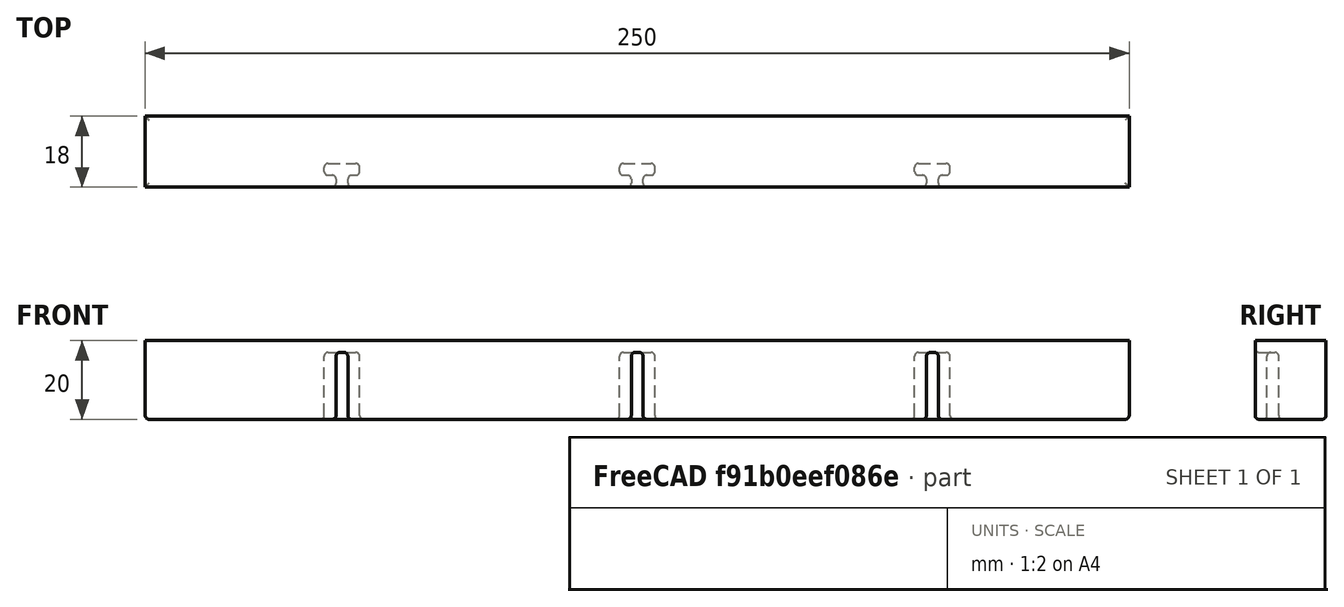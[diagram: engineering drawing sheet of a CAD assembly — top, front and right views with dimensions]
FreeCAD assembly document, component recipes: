
FREECAD ASSEMBLY — COMPONENT RECIPES ("Rack")

This assembly document has 20 components, labeled P0..P19 below (a component is one placed body or linked part). 20 of them carry a construction recipe — the FreeCAD feature program that regenerates the part from scratch, quoted from this document or its linked companion documents; the rest are supplied as boundary geometry only. No exploded tour is included for this assembly.
COMPONENT P0 — recipe-attached ("CenterPanelBottom001", modeled in this document).
Construction recipe (the document's own serialized feature program — sketch geometry with constraints, then the solid features built on it; lengths are millimeters unless a unit is written):

FEATURE [PartDesign::SubShapeBinder] Binder012  label="BinderCenterPanelBottom"
  BindCopyOnChange = 0
  BindMode = 0
  ClaimChildren = false
  Context = -> Body007 [Binder012.]
  Fuse = false
  MakeFace = true
  OffsetFill = false
  OffsetIntersection = false
  OffsetJoinType = 0
  OffsetOpenResult = false
  PartialLoad = false
  Refine = true
  Relative = true
  Support = -> [Sketch]
  _Version = 2
FEATURE [Sketcher::SketchObject] Sketch032  label="SketchCenterPanelBottom"
  ArcFitTolerance = 1e-06
  AttachmentSupport = -> [Origin016]
  ExternalGeometry = -> [Binder012]
  ExternalTypes = [0,0,0,0,0,0]
  FullyConstrained = true
  MakeInternals = false
  MapMode = 5
  sketch-geometry (13):
    g0: LineSegment StartX=-25 StartY=100 StartZ=0 EndX=-25 EndY=-100 EndZ=0
    g1: LineSegment StartX=-25 StartY=-100 StartZ=0 EndX=25 EndY=-100 EndZ=0
    g2: LineSegment StartX=25 StartY=-100 StartZ=0 EndX=25 EndY=100 EndZ=0
    g3: LineSegment StartX=25 StartY=100 StartZ=0 EndX=-25 EndY=100 EndZ=0
    g4: LineSegment [constr] StartX=-20 StartY=-95 StartZ=0 EndX=20 EndY=-95 EndZ=0
    g5: LineSegment [constr] StartX=20 StartY=-95 StartZ=0 EndX=20 EndY=95 EndZ=0
    g6: LineSegment [constr] StartX=20 StartY=95 StartZ=0 EndX=-20 EndY=95 EndZ=0
    g7: LineSegment [constr] StartX=-20 StartY=95 StartZ=0 EndX=-20 EndY=-95 EndZ=0
    g8: GeomPoint [constr] X=0 Y=0 Z=0
    g9: GeomPoint X=-20 Y=95 Z=0
    g10: GeomPoint X=20 Y=95 Z=0
    g11: GeomPoint X=20 Y=-95 Z=0
    g12: GeomPoint X=-20 Y=-95 Z=0
  constraints (26):
    c: Coincident(g0,g1)
    c: Coincident(g1,g2)
    c: Coincident(g2,g3)
    c: Coincident(g3,g0)
    c: Vertical(g0)
    c: Vertical(g2)
    c: Horizontal(g1)
    c: Horizontal(g3)
    c: Coincident(g0,g-7)
    c: Coincident(g1,g-8)
    c: Coincident(g4,g5)
    c: Coincident(g5,g6)
    c: Coincident(g6,g7)
    c: Coincident(g7,g4)
    c: Horizontal(g4)
    c: Horizontal(g6)
    c: Vertical(g5)
    c: Vertical(g7)
    c: Symmetric(g6,g4,g8)
    c: Coincident(g8,g-1)
    c: Distance(g3,g6) = 5
    c: Distance(g2,g5) = 5
    c: Coincident(g9,g6)
    c: Coincident(g10,g5)
    c: Coincident(g11,g4)
    c: Coincident(g12,g4)
FEATURE [PartDesign::Pad] Pad012  label="PadCenterPanelBottom"
  Direction = (0,0,1)
  Length = 20
  Length2 = 10
  Profile = -> Sketch032
  ReferenceAxis = -> Sketch032 [N_Axis]
  Refine = true
  Reversed = true
  SideType = 0
  Suppressed = false
  Type = 0
  Type2 = 0
FEATURE [Sketcher::SketchObject] Sketch033  label="SketchCenterPanelBottomJoints"
  ArcFitTolerance = 1e-06
  AttachmentSupport = -> [Pad012]
  ExternalGeometry = -> [Sketch032]
  ExternalTypes = [0,0,0,0]
  FullyConstrained = true
  MakeInternals = false
  MapMode = 5
  sketch-geometry (40):
    g0: GeomPoint [constr] X=-1.3e-15 Y=100 Z=0
    g1: GeomPoint [constr] X=-4e-16 Y=-100 Z=0
    g2: LineSegment [constr] StartX=-1.5 StartY=100 StartZ=0 EndX=-1.5 EndY=97 EndZ=0
    g3: LineSegment [constr] StartX=-1.5 StartY=97 StartZ=0 EndX=1.5 EndY=97 EndZ=0
    g4: LineSegment [constr] StartX=1.5 StartY=97 StartZ=0 EndX=1.5 EndY=100 EndZ=0
    g5: LineSegment [constr] StartX=1.5 StartY=100 StartZ=0 EndX=-1.5 EndY=100 EndZ=0
    g6: LineSegment [constr] StartX=-4.5 StartY=97 StartZ=0 EndX=-4.5 EndY=94 EndZ=0
    g7: LineSegment [constr] StartX=-4.5 StartY=94 StartZ=0 EndX=4.5 EndY=94 EndZ=0
    g8: LineSegment [constr] StartX=4.5 StartY=94 StartZ=0 EndX=4.5 EndY=97 EndZ=0
    g9: LineSegment [constr] StartX=4.5 StartY=97 StartZ=0 EndX=-4.5 EndY=97 EndZ=0
    g10: GeomPoint [constr] X=-1.3e-15 Y=97 Z=0
    g11: GeomPoint [constr] X=-1.3e-15 Y=97 Z=0
    g12: GeomPoint [constr] X=-1.3e-15 Y=100 Z=0
    g13: LineSegment [constr] StartX=1.5 StartY=-100 StartZ=0 EndX=1.5 EndY=-97 EndZ=0
    g14: LineSegment [constr] StartX=1.5 StartY=-97 StartZ=0 EndX=-1.5 EndY=-97 EndZ=0
    g15: LineSegment [constr] StartX=-1.5 StartY=-97 StartZ=0 EndX=-1.5 EndY=-100 EndZ=0
    g16: LineSegment [constr] StartX=-1.5 StartY=-100 StartZ=0 EndX=1.5 EndY=-100 EndZ=0
    g17: LineSegment [constr] StartX=4.5 StartY=-97 StartZ=0 EndX=4.5 EndY=-94 EndZ=0
    g18: LineSegment [constr] StartX=4.5 StartY=-94 StartZ=0 EndX=-4.5 EndY=-94 EndZ=0
    g19: LineSegment [constr] StartX=-4.5 StartY=-94 StartZ=0 EndX=-4.5 EndY=-97 EndZ=0
    g20: LineSegment [constr] StartX=-4.5 StartY=-97 StartZ=0 EndX=4.5 EndY=-97 EndZ=0
    g21: GeomPoint [constr] X=-4e-16 Y=-97 Z=0
    g22: GeomPoint [constr] X=-4e-16 Y=-97 Z=0
    g23: GeomPoint [constr] X=-4e-16 Y=-100 Z=0
    g24: LineSegment StartX=-1.5 StartY=100 StartZ=0 EndX=1.5 EndY=100 EndZ=0
    g25: LineSegment StartX=1.5 StartY=100 StartZ=0 EndX=1.5 EndY=97 EndZ=0
    g26: LineSegment StartX=1.5 StartY=97 StartZ=0 EndX=4.5 EndY=97 EndZ=0
    g27: LineSegment StartX=4.5 StartY=97 StartZ=0 EndX=4.5 EndY=94 EndZ=0
    g28: LineSegment StartX=4.5 StartY=94 StartZ=0 EndX=-4.5 EndY=94 EndZ=0
    g29: LineSegment StartX=-4.5 StartY=94 StartZ=0 EndX=-4.5 EndY=97 EndZ=0
    g30: LineSegment StartX=-4.5 StartY=97 StartZ=0 EndX=-1.5 EndY=97 EndZ=0
    g31: LineSegment StartX=-1.5 StartY=97 StartZ=0 EndX=-1.5 EndY=100 EndZ=0
    g32: LineSegment StartX=-4.5 StartY=-94 StartZ=0 EndX=4.5 EndY=-94 EndZ=0
    g33: LineSegment StartX=4.5 StartY=-94 StartZ=0 EndX=4.5 EndY=-97 EndZ=0
    g34: LineSegment StartX=4.5 StartY=-97 StartZ=0 EndX=1.5 EndY=-97 EndZ=0
    g35: LineSegment StartX=1.5 StartY=-97 StartZ=0 EndX=1.5 EndY=-100 EndZ=0
    g36: LineSegment StartX=1.5 StartY=-100 StartZ=0 EndX=-1.5 EndY=-100 EndZ=0
    g37: LineSegment StartX=-1.5 StartY=-100 StartZ=0 EndX=-1.5 EndY=-97 EndZ=0
    g38: LineSegment StartX=-1.5 StartY=-97 StartZ=0 EndX=-4.5 EndY=-97 EndZ=0
    g39: LineSegment StartX=-4.5 StartY=-97 StartZ=0 EndX=-4.5 EndY=-94 EndZ=0
  constraints (84):
    c: Symmetric(g-6,g-6,g1)
    c: Symmetric(g-4,g-5,g0)
    c: Coincident(g2,g3)
    c: Coincident(g3,g4)
    c: Coincident(g4,g5)
    c: Coincident(g5,g2)
    c: Vertical(g2)
    c: Vertical(g4)
    c: Horizontal(g3)
    c: Horizontal(g5)
    c: Distance(g2,g4) = 3
    c: Distance(g3,g5) = 3
    c: Coincident(g6,g7)
    c: Coincident(g7,g8)
    c: Coincident(g8,g9)
    c: Coincident(g9,g6)
    c: Vertical(g6)
    c: Vertical(g8)
    c: Horizontal(g7)
    c: Horizontal(g9)
    c: Distance(g6,g8) = 9
    c: Distance(g7,g9) = 3
    c: Symmetric(g6,g8,g10)
    c: Symmetric(g2,g3,g11)
    c: Symmetric(g2,g4,g12)
    c: Coincident(g11,g10)
    c: Coincident(g13,g14)
    c: Coincident(g14,g15)
    c: Coincident(g15,g16)
    c: Coincident(g16,g13)
    c: Distance(g13,g15) = 3
    c: Distance(g14,g16) = 3
    c: Coincident(g17,g18)
    c: Coincident(g18,g19)
    c: Coincident(g19,g20)
    c: Coincident(g20,g17)
    c: Distance(g17,g19) = 9
    c: Distance(g18,g20) = 3
    c: Symmetric(g17,g19,g21)
    c: Symmetric(g13,g14,g22)
    c: Symmetric(g13,g15,g23)
    c: Coincident(g22,g21)
    c: Horizontal(g18)
    c: Horizontal(g20)
    c: Vertical(g17)
    c: Vertical(g19)
    c: Vertical(g15)
    c: Vertical(g13)
    c: Horizontal(g14)
    c: Horizontal(g16)
    c: Coincident(g12,g0)
    c: Coincident(g23,g1)
    c: Coincident(g24,g2)
    c: Coincident(g24,g4)
    c: Coincident(g25,g4)
    c: Coincident(g25,g3)
    c: Coincident(g26,g3)
    c: Coincident(g26,g8)
    c: Coincident(g27,g8)
    c: Coincident(g27,g7)
    c: Coincident(g28,g7)
    c: Coincident(g28,g6)
    c: Coincident(g29,g6)
    c: Coincident(g29,g6)
    c: Coincident(g30,g6)
    c: Coincident(g30,g2)
    c: Coincident(g31,g2)
    c: Coincident(g31,g2)
    c: Coincident(g32,g18)
    c: Coincident(g32,g17)
    c: Coincident(g33,g17)
    c: Coincident(g33,g17)
    c: Coincident(g34,g17)
    c: Coincident(g34,g13)
    c: Coincident(g35,g13)
    c: Coincident(g35,g13)
    c: Coincident(g36,g13)
    c: Coincident(g36,g15)
    c: Coincident(g37,g15)
    c: Coincident(g37,g14)
    c: Coincident(g38,g14)
    c: Coincident(g38,g19)
    c: Coincident(g39,g19)
    c: Coincident(g39,g18)
FEATURE [PartDesign::Pocket] Pocket023  label="PocketCenterPanelBottomJoints"
  BaseFeature = -> Pad012
  Direction = (0,0,-1)
  Length = 5
  Length2 = 5
  Profile = -> Sketch033
  ReferenceAxis = -> Sketch033 [N_Axis]
  Refine = true
  SideType = 0
  Suppressed = false
  Type = 1
  Type2 = 0
FEATURE [Sketcher::SketchObject] Sketch034  label="SketchCenterPanelBottomMidJoints"
  ArcFitTolerance = 1e-06
  AttachmentSupport = -> [Pocket023]
  ExternalGeometry = -> [Sketch032]
  ExternalTypes = [0,0,0,0]
  FullyConstrained = true
  MakeInternals = false
  MapMode = 5
  sketch-geometry (84):
    g0: GeomPoint [constr] X=-1.6e-15 Y=100 Z=0
    g1: GeomPoint [constr] X=0 Y=-100 Z=0
    g2: LineSegment [constr] StartX=0 StartY=-100 StartZ=0 EndX=-1.6e-15 EndY=100 EndZ=0
    g3: LineSegment [constr] StartX=-1.5 StartY=52.8 StartZ=0 EndX=-1.5 EndY=47.2 EndZ=0
    g4: LineSegment [constr] StartX=-1.5 StartY=47.2 StartZ=0 EndX=1.5 EndY=47.2 EndZ=0
    g5: LineSegment [constr] StartX=1.5 StartY=47.2 StartZ=0 EndX=1.5 EndY=52.8 EndZ=0
    g6: LineSegment [constr] StartX=1.5 StartY=52.8 StartZ=0 EndX=-1.5 EndY=52.8 EndZ=0
    g7: LineSegment [constr] StartX=-4.5 StartY=47.2 StartZ=0 EndX=-4.5 EndY=44.2 EndZ=0
    g8: LineSegment [constr] StartX=-4.5 StartY=44.2 StartZ=0 EndX=4.5 EndY=44.2 EndZ=0
    g9: LineSegment [constr] StartX=4.5 StartY=44.2 StartZ=0 EndX=4.5 EndY=47.2 EndZ=0
    g10: LineSegment [constr] StartX=4.5 StartY=47.2 StartZ=0 EndX=-4.5 EndY=47.2 EndZ=0
    g11: LineSegment [constr] StartX=-4.5 StartY=55.8 StartZ=0 EndX=-4.5 EndY=52.8 EndZ=0
    g12: LineSegment [constr] StartX=-4.5 StartY=52.8 StartZ=0 EndX=4.5 EndY=52.8 EndZ=0
    g13: LineSegment [constr] StartX=4.5 StartY=52.8 StartZ=0 EndX=4.5 EndY=55.8 EndZ=0
    g14: LineSegment [constr] StartX=4.5 StartY=55.8 StartZ=0 EndX=-4.5 EndY=55.8 EndZ=0
    g15: GeomPoint [constr] X=1.7e-15 Y=52.8 Z=0
    g16: GeomPoint [constr] X=1.7e-15 Y=47.2 Z=0
    g17: LineSegment [constr] StartX=-1.5 StartY=2.8 StartZ=0 EndX=-1.5 EndY=-2.8 EndZ=0
    g18: LineSegment [constr] StartX=-1.5 StartY=-2.8 StartZ=0 EndX=1.5 EndY=-2.8 EndZ=0
    g19: LineSegment [constr] StartX=1.5 StartY=-2.8 StartZ=0 EndX=1.5 EndY=2.8 EndZ=0
    g20: LineSegment [constr] StartX=1.5 StartY=2.8 StartZ=0 EndX=-1.5 EndY=2.8 EndZ=0
    g21: LineSegment [constr] StartX=-4.5 StartY=-2.8 StartZ=0 EndX=-4.5 EndY=-5.8 EndZ=0
    g22: LineSegment [constr] StartX=-4.5 StartY=-5.8 StartZ=0 EndX=4.5 EndY=-5.8 EndZ=0
    g23: LineSegment [constr] StartX=4.5 StartY=-5.8 StartZ=0 EndX=4.5 EndY=-2.8 EndZ=0
    g24: LineSegment [constr] StartX=4.5 StartY=-2.8 StartZ=0 EndX=-4.5 EndY=-2.8 EndZ=0
    g25: LineSegment [constr] StartX=-4.5 StartY=5.8 StartZ=0 EndX=-4.5 EndY=2.8 EndZ=0
    g26: LineSegment [constr] StartX=-4.5 StartY=2.8 StartZ=0 EndX=4.5 EndY=2.8 EndZ=0
    g27: LineSegment [constr] StartX=4.5 StartY=2.8 StartZ=0 EndX=4.5 EndY=5.8 EndZ=0
    g28: LineSegment [constr] StartX=4.5 StartY=5.8 StartZ=0 EndX=-4.5 EndY=5.8 EndZ=0
    g29: GeomPoint [constr] X=-1e-15 Y=2.8 Z=0
    g30: GeomPoint [constr] X=-1e-15 Y=-2.8 Z=0
    g31: LineSegment [constr] StartX=-1.5 StartY=-47.2 StartZ=0 EndX=-1.5 EndY=-52.8 EndZ=0
    g32: LineSegment [constr] StartX=-1.5 StartY=-52.8 StartZ=0 EndX=1.5 EndY=-52.8 EndZ=0
    g33: LineSegment [constr] StartX=1.5 StartY=-52.8 StartZ=0 EndX=1.5 EndY=-47.2 EndZ=0
    g34: LineSegment [constr] StartX=1.5 StartY=-47.2 StartZ=0 EndX=-1.5 EndY=-47.2 EndZ=0
    g35: LineSegment [constr] StartX=-4.5 StartY=-52.8 StartZ=0 EndX=-4.5 EndY=-55.8 EndZ=0
    g36: LineSegment [constr] StartX=-4.5 StartY=-55.8 StartZ=0 EndX=4.5 EndY=-55.8 EndZ=0
    g37: LineSegment [constr] StartX=4.5 StartY=-55.8 StartZ=0 EndX=4.5 EndY=-52.8 EndZ=0
    g38: LineSegment [constr] StartX=4.5 StartY=-52.8 StartZ=0 EndX=-4.5 EndY=-52.8 EndZ=0
    g39: LineSegment [constr] StartX=-4.5 StartY=-44.2 StartZ=0 EndX=-4.5 EndY=-47.2 EndZ=0
    g40: LineSegment [constr] StartX=-4.5 StartY=-47.2 StartZ=0 EndX=4.5 EndY=-47.2 EndZ=0
    g41: LineSegment [constr] StartX=4.5 StartY=-47.2 StartZ=0 EndX=4.5 EndY=-44.2 EndZ=0
    g42: LineSegment [constr] StartX=4.5 StartY=-44.2 StartZ=0 EndX=-4.5 EndY=-44.2 EndZ=0
    g43: GeomPoint [constr] X=-5e-16 Y=-47.2 Z=0
    g44: GeomPoint [constr] X=-5e-16 Y=-52.8 Z=0
    g45: GeomPoint [constr] X=-1.2e-15 Y=50 Z=0
    g46: GeomPoint [constr] X=-8e-16 Y=-1.7e-15 Z=0
    g47: GeomPoint [constr] X=-4e-16 Y=-50 Z=0
    g48: LineSegment StartX=-4.5 StartY=55.8 StartZ=0 EndX=4.5 EndY=55.8 EndZ=0
    g49: LineSegment StartX=4.5 StartY=55.8 StartZ=0 EndX=4.5 EndY=52.8 EndZ=0
    g50: LineSegment StartX=4.5 StartY=52.8 StartZ=0 EndX=1.5 EndY=52.8 EndZ=0
    g51: LineSegment StartX=1.5 StartY=52.8 StartZ=0 EndX=1.5 EndY=47.2 EndZ=0
    g52: LineSegment StartX=1.5 StartY=47.2 StartZ=0 EndX=4.5 EndY=47.2 EndZ=0
    g53: LineSegment StartX=4.5 StartY=47.2 StartZ=0 EndX=4.5 EndY=44.2 EndZ=0
    g54: LineSegment StartX=4.5 StartY=44.2 StartZ=0 EndX=-4.5 EndY=44.2 EndZ=0
    g55: LineSegment StartX=-4.5 StartY=44.2 StartZ=0 EndX=-4.5 EndY=47.2 EndZ=0
    g56: LineSegment StartX=-4.5 StartY=47.2 StartZ=0 EndX=-1.5 EndY=47.2 EndZ=0
    g57: LineSegment StartX=-1.5 StartY=47.2 StartZ=0 EndX=-1.5 EndY=52.8 EndZ=0
    g58: LineSegment StartX=-1.5 StartY=52.8 StartZ=0 EndX=-4.5 EndY=52.8 EndZ=0
    g59: LineSegment StartX=-4.5 StartY=52.8 StartZ=0 EndX=-4.5 EndY=55.8 EndZ=0
    g60: LineSegment StartX=-4.5 StartY=5.8 StartZ=0 EndX=4.5 EndY=5.8 EndZ=0
    g61: LineSegment StartX=4.5 StartY=5.8 StartZ=0 EndX=4.5 EndY=2.8 EndZ=0
    g62: LineSegment StartX=4.5 StartY=2.8 StartZ=0 EndX=1.5 EndY=2.8 EndZ=0
    g63: LineSegment StartX=1.5 StartY=2.8 StartZ=0 EndX=1.5 EndY=-2.8 EndZ=0
    g64: LineSegment StartX=1.5 StartY=-2.8 StartZ=0 EndX=4.5 EndY=-2.8 EndZ=0
    g65: LineSegment StartX=4.5 StartY=-2.8 StartZ=0 EndX=4.5 EndY=-5.8 EndZ=0
    g66: LineSegment StartX=4.5 StartY=-5.8 StartZ=0 EndX=-4.5 EndY=-5.8 EndZ=0
    g67: LineSegment StartX=-4.5 StartY=-5.8 StartZ=0 EndX=-4.5 EndY=-2.8 EndZ=0
    g68: LineSegment StartX=-4.5 StartY=-2.8 StartZ=0 EndX=-1.5 EndY=-2.8 EndZ=0
    g69: LineSegment StartX=-1.5 StartY=-2.8 StartZ=0 EndX=-1.5 EndY=2.8 EndZ=0
    g70: LineSegment StartX=-1.5 StartY=2.8 StartZ=0 EndX=-4.5 EndY=2.8 EndZ=0
    g71: LineSegment StartX=-4.5 StartY=2.8 StartZ=0 EndX=-4.5 EndY=5.8 EndZ=0
    g72: LineSegment StartX=4.5 StartY=-44.2 StartZ=0 EndX=4.5 EndY=-47.2 EndZ=0
    g73: LineSegment StartX=4.5 StartY=-47.2 StartZ=0 EndX=1.5 EndY=-47.2 EndZ=0
    g74: LineSegment StartX=1.5 StartY=-47.2 StartZ=0 EndX=1.5 EndY=-52.8 EndZ=0
    g75: LineSegment StartX=1.5 StartY=-52.8 StartZ=0 EndX=4.5 EndY=-52.8 EndZ=0
    g76: LineSegment StartX=4.5 StartY=-52.8 StartZ=0 EndX=4.5 EndY=-55.8 EndZ=0
    g77: LineSegment StartX=4.5 StartY=-55.8 StartZ=0 EndX=-4.5 EndY=-55.8 EndZ=0
    g78: LineSegment StartX=-4.5 StartY=-55.8 StartZ=0 EndX=-4.5 EndY=-52.8 EndZ=0
    g79: LineSegment StartX=-4.5 StartY=-52.8 StartZ=0 EndX=-1.5 EndY=-52.8 EndZ=0
    g80: LineSegment StartX=-1.5 StartY=-52.8 StartZ=0 EndX=-1.5 EndY=-47.2 EndZ=0
    g81: LineSegment StartX=-1.5 StartY=-47.2 StartZ=0 EndX=-4.5 EndY=-47.2 EndZ=0
    g82: LineSegment StartX=-4.5 StartY=-47.2 StartZ=0 EndX=-4.5 EndY=-44.2 EndZ=0
    g83: LineSegment StartX=-4.5 StartY=-44.2 StartZ=0 EndX=4.5 EndY=-44.2 EndZ=0
  constraints (187):
    c: Symmetric(g-4,g-5,g0)
    c: Symmetric(g-6,g-6,g1)
    c: Coincident(g2,g1)
    c: Coincident(g2,g0)
    c: Coincident(g3,g4)
    c: Coincident(g4,g5)
    c: Coincident(g5,g6)
    c: Coincident(g6,g3)
    c: Vertical(g3)
    c: Vertical(g5)
    c: Horizontal(g4)
    c: Horizontal(g6)
    c: Distance(g3,g5) = 3
    c: Distance(g4,g6) = 5.6
    c: Coincident(g7,g8)
    c: Coincident(g8,g9)
    c: Coincident(g9,g10)
    c: Coincident(g10,g7)
    c: Vertical(g7)
    c: Vertical(g9)
    c: Horizontal(g8)
    c: Horizontal(g10)
    c: Distance(g7,g9) = 9
    c: Distance(g8,g10) = 3
    c: Coincident(g11,g12)
    c: Coincident(g12,g13)
    c: Coincident(g13,g14)
    c: Coincident(g14,g11)
    c: Vertical(g11)
    c: Vertical(g13)
    c: Horizontal(g12)
    c: Horizontal(g14)
    c: Distance(g11,g13) = 9
    c: Distance(g12,g14) = 3
    c: Symmetric(g3,g4,g16)
    c: Symmetric(g3,g5,g15)
    c: Symmetric(g7,g9,g16)
    c: Symmetric(g11,g12,g15)
    c: Coincident(g17,g18)
    c: Coincident(g31,g32)
    c: Coincident(g18,g19)
    c: Coincident(g32,g33)
    c: Coincident(g19,g20)
    c: Coincident(g33,g34)
    c: Coincident(g20,g17)
    c: Coincident(g34,g31)
    c: Vertical(g17)
    c: Vertical(g31)
    c: Vertical(g19)
    c: Vertical(g33)
    c: Horizontal(g18)
    c: Horizontal(g32)
    c: Horizontal(g20)
    c: Horizontal(g34)
    c: Distance(g17,g19) = 3
    c: Distance(g31,g33) = 3
    c: Distance(g18,g20) = 5.6
    c: Distance(g32,g34) = 5.6
    c: Coincident(g21,g22)
    c: Coincident(g35,g36)
    c: Coincident(g22,g23)
    c: Coincident(g36,g37)
    c: Coincident(g23,g24)
    c: Coincident(g37,g38)
    c: Coincident(g24,g21)
    c: Coincident(g38,g35)
    c: Vertical(g21)
    c: Vertical(g35)
    c: Vertical(g23)
    c: Vertical(g37)
    c: Horizontal(g22)
    c: Horizontal(g36)
    c: Horizontal(g24)
    c: Horizontal(g38)
    c: Distance(g21,g23) = 9
    c: Distance(g35,g37) = 9
    c: Distance(g22,g24) = 3
    c: Distance(g36,g38) = 3
    c: Coincident(g25,g26)
    c: Coincident(g39,g40)
    c: Coincident(g26,g27)
    c: Coincident(g40,g41)
    c: Coincident(g27,g28)
    c: Coincident(g41,g42)
    c: Coincident(g28,g25)
    c: Coincident(g42,g39)
    c: Vertical(g25)
    c: Vertical(g39)
    c: Vertical(g27)
    c: Vertical(g41)
    c: Horizontal(g26)
    c: Horizontal(g40)
    c: Horizontal(g28)
    c: Horizontal(g42)
    c: Distance(g25,g27) = 9
    c: Distance(g39,g41) = 9
    c: Distance(g26,g28) = 3
    c: Distance(g40,g42) = 3
    c: Symmetric(g17,g18,g30)
    c: Symmetric(g31,g32,g44)
    c: Symmetric(g17,g19,g29)
    c: Symmetric(g31,g33,g43)
    c: Symmetric(g21,g23,g30)
    c: Symmetric(g35,g37,g44)
    c: Symmetric(g25,g26,g29)
    c: Symmetric(g39,g40,g43)
    c: Symmetric(g3,g5,g45)
    c: PointOnObject(g45,g2)
    c: Distance(g45,g-4) = 50
    c: Symmetric(g17,g19,g46)
    c: Symmetric(g31,g33,g47)
    c: PointOnObject(g46,g2)
    c: PointOnObject(g47,g2)
    c: Distance(g46,g45) = 50
    c: DistanceY(g47,g46) = 50
    c: Coincident(g48,g11)
    c: Coincident(g48,g13)
    c: Coincident(g49,g13)
    c: Coincident(g49,g12)
    c: Coincident(g50,g12)
    c: Coincident(g50,g5)
    c: Coincident(g51,g5)
    c: Coincident(g51,g4)
    c: Coincident(g52,g4)
    c: Coincident(g52,g9)
    c: Coincident(g53,g9)
    c: Coincident(g53,g8)
    c: Coincident(g54,g8)
    c: Coincident(g54,g7)
    c: Coincident(g55,g7)
    c: Coincident(g55,g7)
    c: Coincident(g56,g7)
    c: Coincident(g56,g3)
    c: Coincident(g57,g3)
    c: Coincident(g57,g3)
    c: Coincident(g58,g3)
    c: Coincident(g58,g11)
    c: Coincident(g59,g11)
    c: Coincident(g59,g11)
    c: Coincident(g60,g25)
    c: Coincident(g60,g27)
    c: Coincident(g61,g27)
    c: Coincident(g61,g26)
    c: Coincident(g62,g26)
    c: Coincident(g62,g19)
    c: Coincident(g63,g19)
    c: Coincident(g63,g18)
    c: Coincident(g64,g18)
    c: Coincident(g64,g23)
    c: Coincident(g65,g23)
    c: Coincident(g65,g22)
    c: Coincident(g66,g22)
    c: Coincident(g66,g21)
    c: Coincident(g67,g21)
    c: Coincident(g67,g21)
    c: Coincident(g68,g21)
    c: Coincident(g68,g17)
    c: Coincident(g69,g17)
    c: Coincident(g69,g17)
    c: Coincident(g70,g17)
    c: Coincident(g70,g25)
    c: Coincident(g71,g25)
    c: Coincident(g71,g25)
    c: Coincident(g72,g41)
    c: Coincident(g72,g40)
    c: Coincident(g73,g40)
    c: Coincident(g73,g33)
    c: Coincident(g74,g33)
    c: Coincident(g74,g32)
    c: Coincident(g75,g32)
    c: Coincident(g75,g37)
    c: Coincident(g76,g37)
    c: Coincident(g76,g36)
    c: Coincident(g77,g36)
    c: Coincident(g77,g35)
    c: Coincident(g78,g35)
    c: Coincident(g78,g35)
    c: Coincident(g79,g35)
    c: Coincident(g79,g31)
    c: Coincident(g80,g31)
    c: Coincident(g80,g31)
    c: Coincident(g81,g31)
    c: Coincident(g81,g39)
    c: Coincident(g82,g39)
    c: Coincident(g82,g39)
    c: Coincident(g83,g39)
    c: Coincident(g83,g41)
FEATURE [PartDesign::Pocket] Pocket024  label="PocketCenterPanelBottomMidJoints"
  BaseFeature = -> Pocket023
  Direction = (0,0,-1)
  Length = 5
  Length2 = 5
  Profile = -> Sketch034
  ReferenceAxis = -> Sketch034 [N_Axis]
  Refine = true
  SideType = 0
  Suppressed = false
  Type = 1
  Type2 = 0
FEATURE [Sketcher::SketchObject] Sketch035  label="SketchCenterPanelBottomCutouts"
  ArcFitTolerance = 1e-06
  AttachmentSupport = -> [Pocket024]
  ExternalGeometry = -> [Pocket024]
  ExternalTypes = [0]
  FullyConstrained = true
  MakeInternals = false
  MapMode = 5
  sketch-geometry (20):
    g0: LineSegment StartX=-20 StartY=60.8 StartZ=0 EndX=20 EndY=60.8 EndZ=0
    g1: LineSegment StartX=20 StartY=60.8 StartZ=0 EndX=20 EndY=89 EndZ=0
    g2: LineSegment StartX=20 StartY=89 StartZ=0 EndX=-20 EndY=89 EndZ=0
    g3: LineSegment StartX=-20 StartY=89 StartZ=0 EndX=-20 EndY=60.8 EndZ=0
    g4: GeomPoint [constr] X=0 Y=74.9 Z=0
    g5: LineSegment StartX=-20 StartY=11 StartZ=0 EndX=20 EndY=11 EndZ=0
    g6: LineSegment StartX=20 StartY=11 StartZ=0 EndX=20 EndY=39.2 EndZ=0
    g7: LineSegment StartX=20 StartY=39.2 StartZ=0 EndX=-20 EndY=39.2 EndZ=0
    g8: LineSegment StartX=-20 StartY=39.2 StartZ=0 EndX=-20 EndY=11 EndZ=0
    g9: GeomPoint [constr] X=0 Y=25.1 Z=0
    g10: LineSegment StartX=-20 StartY=-39 StartZ=0 EndX=20 EndY=-39 EndZ=0
    g11: LineSegment StartX=20 StartY=-39 StartZ=0 EndX=20 EndY=-10.8 EndZ=0
    g12: LineSegment StartX=20 StartY=-10.8 StartZ=0 EndX=-20 EndY=-10.8 EndZ=0
    g13: LineSegment StartX=-20 StartY=-10.8 StartZ=0 EndX=-20 EndY=-39 EndZ=0
    g14: GeomPoint [constr] X=0 Y=-24.9 Z=0
    g15: LineSegment StartX=-20 StartY=-89 StartZ=0 EndX=20 EndY=-89 EndZ=0
    g16: LineSegment StartX=20 StartY=-89 StartZ=0 EndX=20 EndY=-60.8 EndZ=0
    g17: LineSegment StartX=20 StartY=-60.8 StartZ=0 EndX=-20 EndY=-60.8 EndZ=0
    g18: LineSegment StartX=-20 StartY=-60.8 StartZ=0 EndX=-20 EndY=-89 EndZ=0
    g19: GeomPoint [constr] X=0 Y=-74.9 Z=0
  constraints (52):
    c: Coincident(g0,g1)
    c: Coincident(g1,g2)
    c: Coincident(g2,g3)
    c: Coincident(g3,g0)
    c: Horizontal(g0)
    c: Horizontal(g2)
    c: Vertical(g1)
    c: Vertical(g3)
    c: Symmetric(g2,g0,g4)
    c: PointOnObject(g4,g-2)
    c: Distance(g-10,g2) = 5
    c: Distance(g-20,g1) = 5
    c: Distance(g-58,g0) = 5
    c: Coincident(g5,g6)
    c: Coincident(g6,g7)
    c: Coincident(g7,g8)
    c: Coincident(g8,g5)
    c: Horizontal(g5)
    c: Horizontal(g7)
    c: Vertical(g6)
    c: Vertical(g8)
    c: Symmetric(g7,g5,g9)
    c: PointOnObject(g9,g-2)
    c: Equal(g7,g0)
    c: Equal(g1,g6)
    c: Distance(g-52,g7) = 5
    c: Coincident(g10,g11)
    c: Coincident(g11,g12)
    c: Coincident(g12,g13)
    c: Coincident(g13,g10)
    c: Horizontal(g10)
    c: Horizontal(g12)
    c: Vertical(g11)
    c: Vertical(g13)
    c: Symmetric(g12,g10,g14)
    c: PointOnObject(g14,g-2)
    c: Equal(g12,g5)
    c: Equal(g6,g11)
    c: Distance(g-40,g12) = 5
    c: Coincident(g15,g16)
    c: Coincident(g16,g17)
    c: Coincident(g17,g18)
    c: Coincident(g18,g15)
    c: Horizontal(g15)
    c: Horizontal(g17)
    c: Vertical(g16)
    c: Vertical(g18)
    c: Symmetric(g17,g15,g19)
    c: PointOnObject(g19,g-2)
    c: Equal(g10,g17)
    c: Equal(g16,g11)
    c: Distance(g-29,g17) = 5
FEATURE [PartDesign::Pocket] Pocket025  label="PocketCenterPanelBottomCutouts"
  BaseFeature = -> Pocket024
  Direction = (0,0,-1)
  Length = 5
  Length2 = 5
  Profile = -> Sketch035
  ReferenceAxis = -> Sketch035 [N_Axis]
  Refine = true
  SideType = 0
  Suppressed = false
  Type = 1
  Type2 = 0
FEATURE [PartDesign::Hole] Hole010
  BaseFeature = -> Pocket025
  BaseProfileType = 7
  CustomThreadClearance = 0
  Depth = 25
  DepthType = 0
  Diameter = 3.7
  DrillForDepth = false
  DrillPoint = 1
  DrillPointAngle = 118
  HoleCutCountersinkAngle = 90
  HoleCutCustomValues = false
  HoleCutDepth = 0
  HoleCutDiameter = 0
  HoleCutType = 0
  ModelThread = false
  Profile = -> Sketch032 [Vertex6,Vertex5,Vertex7,Vertex8]
  Refine = true
  Suppressed = false
  Tapered = false
  TaperedAngle = 90
  ThreadClass = 0
  ThreadDepth = 25
  ThreadDepthType = 0
  ThreadDiameter = 4.5
  ThreadDirection = 0
  ThreadFit = 0
  ThreadSize = 12
  ThreadType = 1
  Threaded = true
  UseCustomThreadClearance = false
FEATURE [Sketcher::SketchObject] Sketch061
  ArcFitTolerance = 1e-06
  AttachmentSupport = -> [Origin016]
  ExternalGeometry = -> [Sketch035]
  ExternalTypes = [0,0,0,0,0,0,0,0,0,0,0,0,0,0,0,0]
  FullyConstrained = true
  MakeInternals = false
  MapMode = 5
  sketch-geometry (12):
    g0: GeomPoint [constr] X=1.8e-15 Y=74.9 Z=0
    g1: GeomPoint [constr] X=-2.2e-15 Y=25.1 Z=0
    g2: GeomPoint [constr] X=0 Y=-24.9 Z=0
    g3: GeomPoint [constr] X=3.1e-15 Y=-74.9 Z=0
    g4: LineSegment StartX=-13.5 StartY=91.4 StartZ=0 EndX=-13.5 EndY=58.4 EndZ=0
    g5: LineSegment StartX=-13.5 StartY=58.4 StartZ=0 EndX=13.5 EndY=58.4 EndZ=0
    g6: LineSegment StartX=13.5 StartY=58.4 StartZ=0 EndX=13.5 EndY=91.4 EndZ=0
    g7: LineSegment StartX=13.5 StartY=91.4 StartZ=0 EndX=-13.5 EndY=91.4 EndZ=0
    g8: LineSegment StartX=-13.5 StartY=41.6 StartZ=0 EndX=-13.5 EndY=8.6 EndZ=0
    g9: LineSegment StartX=-13.5 StartY=8.6 StartZ=0 EndX=13.5 EndY=8.6 EndZ=0
    g10: LineSegment StartX=13.5 StartY=8.6 StartZ=0 EndX=13.5 EndY=41.6 EndZ=0
    g11: LineSegment StartX=13.5 StartY=41.6 StartZ=0 EndX=-13.5 EndY=41.6 EndZ=0
  constraints (26):
    c: Symmetric(g-18,g-16,g3)
    c: Symmetric(g-14,g-12,g2)
    c: Symmetric(g-9,g-10,g1)
    c: Symmetric(g-6,g-5,g0)
    c: Coincident(g4,g5)
    c: Coincident(g5,g6)
    c: Coincident(g6,g7)
    c: Coincident(g7,g4)
    c: Vertical(g4)
    c: Vertical(g6)
    c: Horizontal(g5)
    c: Horizontal(g7)
    c: Distance(g4,g6) = 27
    c: Distance(g5,g7) = 33
    c: Coincident(g8,g9)
    c: Coincident(g9,g10)
    c: Coincident(g10,g11)
    c: Coincident(g11,g8)
    c: Vertical(g8)
    c: Vertical(g10)
    c: Horizontal(g9)
    c: Horizontal(g11)
    c: Equal(g11,g5)
    c: Equal(g10,g6)
    c: Symmetric(g4,g6,g0)
    c: Symmetric(g8,g10,g1)
FEATURE [PartDesign::Pocket] Pocket045
  BaseFeature = -> Hole010
  Direction = (0,0,-1)
  Length = 5
  Length2 = 5
  Profile = -> Sketch061
  ReferenceAxis = -> Sketch061 [N_Axis]
  Refine = true
  SideType = 0
  Suppressed = false
  Type = 1
  Type2 = 0
FEATURE [PartDesign::Fillet] Fillet035
  Base = -> Pocket045 [Edge1,Edge2,Edge3,Edge4,Edge5,Edge6,Edge7,Edge8,Edge9,Edge10,Edge11,Edge12,Edge13,Edge14,Edge15,Edge16,Edge17,Edge18,Edge19,Edge20,Edge21,Edge22,Edge23,Edge24,Edge25,Edge26,Edge27,Edge28,Edge29,Edge30,Edge31,Edge32,Edge33,Edge34,Edge35,Edge36,Edge37,Edge38,Edge39,Edge40,+236 more]
  BaseFeature = -> Pocket045
  Radius = 1
  Refine = true
  SupportTransform = false
  Suppressed = false
  UseAllEdges = true
FEATURE [PartDesign::Body] Body007  label="CenterPanelBottom"
  AllowCompound = true
  Group = -> [Binder012,Sketch032,Pad012,Sketch033,Pocket023,Sketch034,Pocket024,Sketch035,Pocket025,Hole010,Sketch061,Pocket045,Fillet035]
  Origin = -> Origin016
  Tip = -> Fillet035
COMPONENT P1 — recipe-attached ("CenterPanelTop001", modeled in this document).
Construction recipe (the document's own serialized feature program — sketch geometry with constraints, then the solid features built on it; lengths are millimeters unless a unit is written):

FEATURE [PartDesign::SubShapeBinder] Binder014  label="BinderCenterPanelTop"
  BindCopyOnChange = 0
  BindMode = 0
  ClaimChildren = false
  Context = -> Body008 [Binder014.]
  Fuse = false
  MakeFace = true
  OffsetFill = false
  OffsetIntersection = false
  OffsetJoinType = 0
  OffsetOpenResult = false
  PartialLoad = false
  Refine = true
  Relative = true
  Support = -> [Body007[Sketch026.]]
  _Version = 2
FEATURE [Sketcher::SketchObject] Sketch031  label="SketchCenterPanelTop"
  ArcFitTolerance = 1e-06
  AttachmentSupport = -> [Origin018]
  ExternalGeometry = -> [Binder014]
  ExternalTypes = [0]
  FullyConstrained = true
  MakeInternals = false
  MapMode = 5
  sketch-geometry (9):
    g0: LineSegment [constr] StartX=-20 StartY=-95 StartZ=0 EndX=20 EndY=-95 EndZ=0
    g1: LineSegment [constr] StartX=20 StartY=-95 StartZ=0 EndX=20 EndY=95 EndZ=0
    g2: LineSegment [constr] StartX=20 StartY=95 StartZ=0 EndX=-20 EndY=95 EndZ=0
    g3: LineSegment [constr] StartX=-20 StartY=95 StartZ=0 EndX=-20 EndY=-95 EndZ=0
    g4: GeomPoint [constr] X=0 Y=0 Z=0
    g5: GeomPoint X=-20 Y=95 Z=0
    g6: GeomPoint X=20 Y=95 Z=0
    g7: GeomPoint X=20 Y=-95 Z=0
    g8: GeomPoint X=-20 Y=-95 Z=0
  constraints (16):
    c: Coincident(g0,g1)
    c: Coincident(g1,g2)
    c: Coincident(g2,g3)
    c: Coincident(g3,g0)
    c: Horizontal(g0)
    c: Horizontal(g2)
    c: Vertical(g1)
    c: Vertical(g3)
    c: Symmetric(g2,g0,g4)
    c: Coincident(g4,g-1)
    c: Distance(g-6,g2) = 5
    c: Distance(g-5,g1) = 5
    c: Coincident(g5,g2)
    c: Coincident(g6,g1)
    c: Coincident(g7,g0)
    c: Coincident(g8,g0)
FEATURE [PartDesign::Pad] Pad011  label="PadCenterPanelTop"
  Direction = (0,0,1)
  Length = 3
  Length2 = 10
  Profile = -> Sketch031
  ReferenceAxis = -> Sketch031 [N_Axis]
  Refine = true
  Reversed = true
  SideType = 0
  Suppressed = false
  Type = 0
  Type2 = 0
FEATURE [PartDesign::Hole] Hole009
  BaseFeature = -> Pad011
  BaseProfileType = 7
  CustomThreadClearance = 0
  Depth = 25
  DepthType = 0
  Diameter = 4.5
  DrillForDepth = false
  DrillPoint = 1
  DrillPointAngle = 118
  HoleCutCountersinkAngle = 90
  HoleCutCustomValues = false
  HoleCutDepth = 4
  HoleCutDiameter = 8
  HoleCutType = 2
  ModelThread = false
  Profile = -> Sketch031 [Vertex5,Vertex6,Vertex7,Vertex8]
  Refine = true
  Suppressed = false
  Tapered = false
  TaperedAngle = 90
  ThreadClass = 0
  ThreadDepth = 25
  ThreadDepthType = 0
  ThreadDiameter = 4
  ThreadDirection = 0
  ThreadFit = 0
  ThreadSize = 11
  ThreadType = 1
  Threaded = false
  UseCustomThreadClearance = false
FEATURE [Sketcher::SketchObject] Sketch051
  ArcFitTolerance = 1e-06
  AttachmentSupport = -> [Origin018]
  ExternalGeometry = -> [Hole009]
  ExternalTypes = [0]
  FullyConstrained = true
  MakeInternals = false
  MapMode = 5
  sketch-geometry (34):
    g0: LineSegment [constr] StartX=-25 StartY=50 StartZ=0 EndX=25 EndY=50 EndZ=0
    g1: LineSegment [constr] StartX=-25 StartY=-7.9e-15 StartZ=0 EndX=25 EndY=-7.9e-15 EndZ=0
    g2: LineSegment [constr] StartX=-25 StartY=-50 StartZ=0 EndX=25 EndY=-50 EndZ=0
    g3: GeomPoint [constr] X=-6e-16 Y=75 Z=0
    g4: GeomPoint [constr] X=-5e-16 Y=25 Z=0
    g5: GeomPoint [constr] X=-1.7e-15 Y=-25 Z=0
    g6: GeomPoint [constr] X=-1.1e-15 Y=-75 Z=0
    g7: Circle CenterX=-5e-16 CenterY=25 CenterZ=0 NormalX=0 NormalY=0 NormalZ=1 AngleXU=0 Radius=11.85
    g8: Circle CenterX=-1.7e-15 CenterY=-25 CenterZ=0 NormalX=0 NormalY=0 NormalZ=1 AngleXU=0 Radius=3.5
    g9: Circle CenterX=-1.1e-15 CenterY=-75 CenterZ=0 NormalX=0 NormalY=0 NormalZ=1 AngleXU=0 Radius=3.5
    g10: LineSegment [constr] StartX=12.5 StartY=10 StartZ=0 EndX=12.5 EndY=40 EndZ=0
    g11: LineSegment [constr] StartX=12.5 StartY=40 StartZ=0 EndX=-12.5 EndY=40 EndZ=0
    g12: LineSegment [constr] StartX=-12.5 StartY=40 StartZ=0 EndX=-12.5 EndY=10 EndZ=0
    g13: LineSegment [constr] StartX=-12.5 StartY=10 StartZ=0 EndX=12.5 EndY=10 EndZ=0
    g14: LineSegment [constr] StartX=-11.5 StartY=11 StartZ=0 EndX=11.5 EndY=11 EndZ=0
    g15: LineSegment [constr] StartX=11.5 StartY=11 StartZ=0 EndX=11.5 EndY=39 EndZ=0
    g16: LineSegment [constr] StartX=11.5 StartY=39 StartZ=0 EndX=-11.5 EndY=39 EndZ=0
    g17: LineSegment [constr] StartX=-11.5 StartY=39 StartZ=0 EndX=-11.5 EndY=11 EndZ=0
    g18: GeomPoint [constr] X=-5e-16 Y=25 Z=0
    g19: Circle CenterX=-9.5 CenterY=37 CenterZ=0 NormalX=0 NormalY=0 NormalZ=1 AngleXU=0 Radius=2
    g20: Circle CenterX=9.5 CenterY=13 CenterZ=0 NormalX=0 NormalY=0 NormalZ=1 AngleXU=0 Radius=2
    g21: LineSegment [constr] StartX=-12.5 StartY=60 StartZ=0 EndX=12.5 EndY=60 EndZ=0
    g22: LineSegment [constr] StartX=12.5 StartY=60 StartZ=0 EndX=12.5 EndY=90 EndZ=0
    g23: LineSegment [constr] StartX=12.5 StartY=90 StartZ=0 EndX=-12.5 EndY=90 EndZ=0
    g24: LineSegment [constr] StartX=-12.5 StartY=90 StartZ=0 EndX=-12.5 EndY=60 EndZ=0
    g25: GeomPoint [constr] X=-6e-16 Y=75 Z=0
    g26: LineSegment [constr] StartX=-11.5 StartY=61 StartZ=0 EndX=11.5 EndY=61 EndZ=0
    g27: LineSegment [constr] StartX=11.5 StartY=61 StartZ=0 EndX=11.5 EndY=89 EndZ=0
    g28: LineSegment [constr] StartX=11.5 StartY=89 StartZ=0 EndX=-11.5 EndY=89 EndZ=0
    g29: LineSegment [constr] StartX=-11.5 StartY=89 StartZ=0 EndX=-11.5 EndY=61 EndZ=0
    g30: GeomPoint [constr] X=-6e-16 Y=75 Z=0
    g31: Circle CenterX=-6e-16 CenterY=75 CenterZ=0 NormalX=0 NormalY=0 NormalZ=1 AngleXU=0 Radius=11.85
    g32: Circle CenterX=-9.5 CenterY=87 CenterZ=0 NormalX=0 NormalY=0 NormalZ=1 AngleXU=0 Radius=2
    g33: Circle CenterX=9.5 CenterY=63 CenterZ=0 NormalX=0 NormalY=0 NormalZ=1 AngleXU=0 Radius=2
  constraints (83):
    c: PointOnObject(g0,g-3)
    c: PointOnObject(g0,g-6)
    c: Horizontal(g0)
    c: Distance(g-4,g0) = 50
    c: PointOnObject(g1,g-3)
    c: PointOnObject(g1,g-6)
    c: Horizontal(g1)
    c: PointOnObject(g2,g-3)
    c: PointOnObject(g2,g-6)
    c: Horizontal(g2)
    c: Distance(g0,g1) = 50
    c: Distance(g1,g2) = 50
    c: Symmetric(g0,g-6,g3)
    c: Symmetric(g1,g0,g4)
    c: Symmetric(g2,g1,g5)
    c: Symmetric(g-5,g2,g6)
    c: Diameter(g7) = 23.7
    c: Coincident(g7,g4)
    c: Diameter(g8) = 7
    c: Coincident(g8,g5)
    c: Diameter(g9) = 7
    c: Coincident(g9,g6)
    c: Coincident(g10,g11)
    c: Coincident(g11,g12)
    c: Coincident(g12,g13)
    c: Coincident(g13,g10)
    c: Vertical(g10)
    c: Vertical(g12)
    c: Horizontal(g11)
    c: Horizontal(g13)
    c: Symmetric(g12,g10,g4)
    c: DistanceX(g11,g11) = 25
    c: DistanceY(g10,g10) = 30
    c: Coincident(g14,g15)
    c: Coincident(g15,g16)
    c: Coincident(g16,g17)
    c: Coincident(g17,g14)
    c: Horizontal(g14)
    c: Horizontal(g16)
    c: Vertical(g15)
    c: Vertical(g17)
    c: Symmetric(g16,g14,g18)
    c: Coincident(g18,g4)
    c: Distance(g11,g16) = 1
    c: Distance(g10,g15) = 1
    c: Diameter(g19) = 4
    c: Tangent(g19,g16)
    c: Tangent(g19,g17)
    c: Tangent(g20,g14)
    c: Tangent(g20,g15)
    c: Equal(g20,g19)
    c: Coincident(g21,g22)
    c: Coincident(g22,g23)
    c: Coincident(g23,g24)
    c: Coincident(g24,g21)
    c: Horizontal(g21)
    c: Horizontal(g23)
    c: Vertical(g22)
    c: Vertical(g24)
    c: Symmetric(g23,g21,g25)
    c: Coincident(g25,g3)
    c: Coincident(g26,g27)
    c: Coincident(g27,g28)
    c: Coincident(g28,g29)
    c: Coincident(g29,g26)
    c: Horizontal(g26)
    c: Horizontal(g28)
    c: Vertical(g27)
    c: Vertical(g29)
    c: Symmetric(g28,g26,g30)
    c: Coincident(g30,g3)
    c: Equal(g23,g11)
    c: Equal(g22,g10)
    c: Equal(g27,g15)
    c: Equal(g28,g16)
    c: Coincident(g31,g3)
    c: Equal(g31,g7)
    c: Equal(g32,g33)
    c: Equal(g33,g19)
    c: Tangent(g32,g28)
    c: Tangent(g32,g29)
    c: Tangent(g33,g26)
    c: Tangent(g27,g33)
FEATURE [PartDesign::Pocket] Pocket038
  BaseFeature = -> Hole009
  Direction = (0,0,-1)
  Length = 5
  Length2 = 5
  Profile = -> Sketch051
  ReferenceAxis = -> Sketch051 [N_Axis]
  Refine = true
  SideType = 0
  Suppressed = false
  Type = 0
  Type2 = 0
FEATURE [PartDesign::Body] Body008  label="CenterPanelTop-Ethernet2-SMA2"
  AllowCompound = true
  Group = -> [Sketch031,Binder014,Pad011,Hole009,Sketch051,Pocket038]
  Origin = -> Origin018
  Tip = -> Pocket038
COMPONENT P2 — recipe-attached ("Connector5Way", modeled in this document).
Construction recipe (the document's own serialized feature program — sketch geometry with constraints, then the solid features built on it; lengths are millimeters unless a unit is written):

FEATURE [PartDesign::SubShapeBinder] Binder001
  BindCopyOnChange = 0
  BindMode = 0
  ClaimChildren = false
  Context = -> Body001 [Binder001.]
  Fuse = false
  MakeFace = true
  OffsetFill = false
  OffsetIntersection = false
  OffsetJoinType = 0
  OffsetOpenResult = false
  PartialLoad = false
  Refine = true
  Relative = true
  Support = -> [Sketch]
  _Version = 2
FEATURE [Sketcher::SketchObject] Sketch004
  ArcFitTolerance = 1e-06
  AttachmentSupport = -> [Origin002]
  ExternalGeometry = -> [Binder001]
  ExternalTypes = [0,0,0,0,0,0,0,0,0]
  FullyConstrained = true
  MakeInternals = false
  MapMode = 5
  sketch-geometry (1):
    g0: LineSegment StartX=-25 StartY=0 StartZ=0 EndX=-25 EndY=-100 EndZ=0
  constraints (2):
    c: Coincident(g0,g-4)
    c: Coincident(g0,g-6)
FEATURE [PartDesign::Pad] Pad002
  Direction = (0,0,1)
  Length = 3
  Length2 = 10
  Profile = -> Sketch004
  ReferenceAxis = -> Sketch004 [N_Axis]
  Refine = true
  Reversed = true
  SideType = 0
  Suppressed = false
  Type = 0
  Type2 = 0
FEATURE [PartDesign::Hole] Hole001  label="HolesOutside"
  BaseFeature = -> Pad002
  BaseProfileType = 7
  CustomThreadClearance = 0
  Depth = 10
  DepthType = 0
  Diameter = 4.5
  DrillForDepth = false
  DrillPoint = 1
  DrillPointAngle = 118
  HoleCutCountersinkAngle = 90
  HoleCutCustomValues = false
  HoleCutDepth = 4
  HoleCutDiameter = 8
  HoleCutType = 2
  ModelThread = false
  Profile = -> Pad002 [Face8,Face7,Face6,Face5]
  Refine = true
  Suppressed = false
  Tapered = false
  TaperedAngle = 90
  ThreadClass = 0
  ThreadDepth = 10
  ThreadDepthType = 0
  ThreadDiameter = 4
  ThreadDirection = 0
  ThreadFit = 0
  ThreadSize = 11
  ThreadType = 1
  Threaded = false
  UseCustomThreadClearance = false
FEATURE [PartDesign::Hole] Hole002  label="HolesInside"
  BaseFeature = -> Hole001
  BaseProfileType = 7
  CustomThreadClearance = 0
  Depth = 3
  DepthType = 0
  Diameter = 4.5
  DrillForDepth = false
  DrillPoint = 1
  DrillPointAngle = 118
  HoleCutCountersinkAngle = 90
  HoleCutCustomValues = false
  HoleCutDepth = 0
  HoleCutDiameter = 0
  HoleCutType = 0
  ModelThread = false
  Profile = -> Binder001 [Edge45,Edge46,Edge47,Edge48]
  Refine = true
  Suppressed = false
  Tapered = false
  TaperedAngle = 90
  ThreadClass = 0
  ThreadDepth = 3
  ThreadDepthType = 0
  ThreadDiameter = 4
  ThreadDirection = 0
  ThreadFit = 0
  ThreadSize = 11
  ThreadType = 1
  Threaded = false
  UseCustomThreadClearance = false
FEATURE [PartDesign::Pocket] Pocket002
  BaseFeature = -> Hole002
  Direction = (0,0,-1)
  Length = 5
  Length2 = 5
  Profile = -> Binder001 [Edge49]
  Refine = true
  SideType = 0
  Suppressed = false
  Type = 0
  Type2 = 0
FEATURE [Sketcher::SketchObject] Sketch005  label="SketchBottomInner"
  ArcFitTolerance = 1e-06
  AttachmentSupport = -> [Pocket002]
  ExternalGeometry = -> [Binder001]
  ExternalTypes = [0,0,0,0]
  FullyConstrained = true
  MakeInternals = false
  MapMode = 5
  Placement = pos=(0,0,-3) rot=(1,0,0;3.14159rad)
FEATURE [PartDesign::Fillet] Fillet012
  Base = -> Pocket002 [Face11,Face12,Face14,Face10,Face8]
  BaseFeature = -> Pocket002
  Radius = 1
  Refine = true
  SupportTransform = false
  Suppressed = false
  UseAllEdges = false
FEATURE [PartDesign::Body] Body001  label="Fan Right Top"
  AllowCompound = true
  Group = -> [Binder001,Sketch004,Pad002,Hole001,Hole002,Pocket002,Sketch005,Fillet012]
  Origin = -> Origin002
  Tip = -> Fillet012
COMPONENT P3 — same part as P2; its construction recipe is shown at P2.
COMPONENT P4 — same part as P2; its construction recipe is shown at P2.
COMPONENT P5 — same part as P2; its construction recipe is shown at P2.
COMPONENT P6 — same part as P2; its construction recipe is shown at P2.
COMPONENT P7 — same part as P2; its construction recipe is shown at P2.
COMPONENT P8 — recipe-attached ("Fan Bottom001", modeled in this document).
Construction recipe (the document's own serialized feature program — sketch geometry with constraints, then the solid features built on it; lengths are millimeters unless a unit is written):

FEATURE [PartDesign::SubShapeBinder] Binder008
  BindCopyOnChange = 0
  BindMode = 0
  ClaimChildren = false
  Context = -> Body003 [Binder008.]
  Fuse = false
  MakeFace = true
  OffsetFill = false
  OffsetIntersection = false
  OffsetJoinType = 0
  OffsetOpenResult = false
  PartialLoad = false
  Refine = true
  Relative = true
  Support = -> [Sketch]
  _Version = 2
FEATURE [Sketcher::SketchObject] Sketch012  label="SketchFanBottom"
  ArcFitTolerance = 1e-06
  AttachmentSupport = -> [Origin008]
  ExternalGeometry = -> [Binder008]
  ExternalTypes = [0,0,0,0,0,0,0,0,0,0,0,0,0]
  FullyConstrained = true
  MakeInternals = false
  MapMode = 5
  sketch-geometry (1):
    g0: LineSegment StartX=-25 StartY=0 StartZ=0 EndX=-25 EndY=-100 EndZ=0
  constraints (2):
    c: Coincident(g0,g-3)
    c: Coincident(g0,g-5)
FEATURE [PartDesign::Pad] Pad005  label="PadBody001"
  Direction = (0,0,1)
  Length = 32
  Length2 = 10
  Profile = -> Sketch012 [Edge4,Edge5,Edge3,Edge2,Edge1,Edge8,Edge7,Edge6,Edge9]
  ReferenceAxis = -> Sketch012 [N_Axis]
  Refine = true
  Reversed = true
  SideType = 0
  Suppressed = false
  Type = 0
  Type2 = 0
FEATURE [PartDesign::Hole] Hole004  label="HoleScrews001"
  BaseFeature = -> Pad005
  BaseProfileType = 7
  CustomThreadClearance = 0
  Depth = 292.893
  DepthType = 1
  Diameter = 3.7
  DrillForDepth = false
  DrillPoint = 1
  DrillPointAngle = 118
  HoleCutCountersinkAngle = 90
  HoleCutCustomValues = false
  HoleCutDepth = 0
  HoleCutDiameter = 0
  HoleCutType = 0
  ModelThread = false
  Profile = -> Sketch012 [Edge13,Edge10,Edge11,Edge12]
  Refine = true
  Suppressed = false
  Tapered = false
  TaperedAngle = 90
  ThreadClass = 0
  ThreadDepth = 292.893
  ThreadDepthType = 0
  ThreadDiameter = 4.5
  ThreadDirection = 0
  ThreadFit = 0
  ThreadSize = 12
  ThreadType = 1
  Threaded = true
  UseCustomThreadClearance = false
FEATURE [Sketcher::SketchObject] Sketch013  label="SketchJointTop"
  ArcFitTolerance = 1e-06
  AttachmentSupport = -> [Origin008]
  ExternalGeometry = -> [Sketch012]
  ExternalTypes = [0,0,0,0,0,0,0]
  FullyConstrained = true
  MakeInternals = false
  MapMode = 5
  sketch-geometry (21):
    g0: LineSegment [constr] StartX=-35 StartY=-10 StartZ=0 EndX=-35 EndY=0 EndZ=0
    g1: GeomPoint [constr] X=-75 Y=-5 Z=0
    g2: LineSegment [constr] StartX=-75 StartY=0 StartZ=0 EndX=-75 EndY=-100 EndZ=0
    g3: LineSegment [constr] StartX=-79.5 StartY=-3 StartZ=0 EndX=-79.5 EndY=-6 EndZ=0
    g4: LineSegment [constr] StartX=-79.5 StartY=-6 StartZ=0 EndX=-70.5 EndY=-6 EndZ=0
    g5: LineSegment [constr] StartX=-70.5 StartY=-6 StartZ=0 EndX=-70.5 EndY=-3 EndZ=0
    g6: LineSegment [constr] StartX=-70.5 StartY=-3 StartZ=0 EndX=-79.5 EndY=-3 EndZ=0
    g7: LineSegment [constr] StartX=-76.5 StartY=0 StartZ=0 EndX=-76.5 EndY=-6 EndZ=0
    g8: LineSegment [constr] StartX=-76.5 StartY=-6 StartZ=0 EndX=-73.5 EndY=-6 EndZ=0
    g9: LineSegment [constr] StartX=-73.5 StartY=-6 StartZ=0 EndX=-73.5 EndY=0 EndZ=0
    g10: LineSegment [constr] StartX=-73.5 StartY=0 StartZ=0 EndX=-76.5 EndY=0 EndZ=0
    g11: LineSegment StartX=-76.5 StartY=0 StartZ=0 EndX=-73.5 EndY=0 EndZ=0
    g12: GeomPoint X=-73.5 Y=-3 Z=0
    g13: GeomPoint X=-76.5 Y=-3 Z=0
    g14: LineSegment StartX=-73.5 StartY=0 StartZ=0 EndX=-73.5 EndY=-3 EndZ=0
    g15: LineSegment StartX=-73.5 StartY=-3 StartZ=0 EndX=-70.5 EndY=-3 EndZ=0
    g16: LineSegment StartX=-70.5 StartY=-3 StartZ=0 EndX=-70.5 EndY=-6 EndZ=0
    g17: LineSegment StartX=-70.5 StartY=-6 StartZ=0 EndX=-79.5 EndY=-6 EndZ=0
    g18: LineSegment StartX=-79.5 StartY=-6 StartZ=0 EndX=-79.5 EndY=-3 EndZ=0
    g19: LineSegment StartX=-79.5 StartY=-3 StartZ=0 EndX=-76.5 EndY=-3 EndZ=0
    g20: LineSegment StartX=-76.5 StartY=-3 StartZ=0 EndX=-76.5 EndY=0 EndZ=0
  constraints (52):
    c: Coincident(g0,g-8)
    c: PointOnObject(g0,g-5)
    c: Vertical(g0)
    c: Symmetric(g-8,g0,g1)
    c: Vertical(g2)
    c: PointOnObject(g1,g2)
    c: PointOnObject(g2,g-6)
    c: PointOnObject(g2,g-5)
    c: Coincident(g3,g4)
    c: Coincident(g4,g5)
    c: Coincident(g5,g6)
    c: Coincident(g6,g3)
    c: Vertical(g3)
    c: Vertical(g5)
    c: Horizontal(g4)
    c: Horizontal(g6)
    c: Coincident(g7,g8)
    c: Coincident(g8,g9)
    c: Coincident(g9,g10)
    c: Coincident(g10,g7)
    c: Vertical(g7)
    c: Vertical(g9)
    c: Horizontal(g8)
    c: Horizontal(g10)
    c: DistanceX(g10,g10) = 3
    c: DistanceY(g9,g9) = 6
    c: Equal(g5,g10)
    c: DistanceX(g4,g4) = 9
    c: PointOnObject(g7,g4)
    c: Distance(g7,g3) = 3
    c: PointOnObject(g2,g10)
    c: Distance(g2,g7) = 1.5
    c: Coincident(g11,g7)
    c: Coincident(g11,g9)
    c: PointOnObject(g12,g6)
    c: PointOnObject(g12,g9)
    c: PointOnObject(g13,g6)
    c: PointOnObject(g13,g7)
    c: Coincident(g14,g9)
    c: Coincident(g14,g12)
    c: Coincident(g15,g12)
    c: Coincident(g15,g5)
    c: Coincident(g16,g5)
    c: Coincident(g16,g4)
    c: Coincident(g17,g4)
    c: Coincident(g17,g3)
    c: Coincident(g18,g3)
    c: Coincident(g18,g3)
    c: Coincident(g19,g3)
    c: Coincident(g19,g13)
    c: Coincident(g20,g13)
    c: Coincident(g20,g7)
FEATURE [PartDesign::Pocket] Pocket014  label="PocketJointTop"
  BaseFeature = -> Hole004
  Direction = (0,0,-1)
  Length = 25
  Length2 = 5
  Profile = -> Sketch013
  ReferenceAxis = -> Sketch013 [N_Axis]
  Refine = true
  SideType = 0
  Suppressed = false
  Type = 3
  Type2 = 0
  UpToFace = -> Hole004 [Face5]
FEATURE [Sketcher::SketchObject] Sketch014  label="SketchJointBottom"
  ArcFitTolerance = 1e-06
  AttachmentSupport = -> [Pocket014]
  ExternalGeometry = -> [Sketch013,Binder008]
  ExternalTypes = [0,0,0,0,0,0,0,0,0,0]
  FullyConstrained = true
  MakeInternals = false
  MapMode = 5
  sketch-geometry (21):
    g0: LineSegment [constr] StartX=-115 StartY=-90 StartZ=0 EndX=-115 EndY=-100 EndZ=0
    g1: GeomPoint [constr] X=-75 Y=-95 Z=0
    g2: LineSegment [constr] StartX=-75 StartY=-95 StartZ=0 EndX=-75 EndY=-100 EndZ=0
    g3: LineSegment [constr] StartX=-76.5 StartY=-100 StartZ=0 EndX=-73.5 EndY=-100 EndZ=0
    g4: LineSegment [constr] StartX=-73.5 StartY=-100 StartZ=0 EndX=-73.5 EndY=-97 EndZ=0
    g5: LineSegment [constr] StartX=-73.5 StartY=-97 StartZ=0 EndX=-76.5 EndY=-97 EndZ=0
    g6: LineSegment [constr] StartX=-76.5 StartY=-97 StartZ=0 EndX=-76.5 EndY=-100 EndZ=0
    g7: GeomPoint [constr] X=-75 Y=-98.5 Z=0
    g8: LineSegment [constr] StartX=-79.5 StartY=-94 StartZ=0 EndX=-79.5 EndY=-97 EndZ=0
    g9: LineSegment [constr] StartX=-79.5 StartY=-97 StartZ=0 EndX=-70.5 EndY=-97 EndZ=0
    g10: LineSegment [constr] StartX=-70.5 StartY=-97 StartZ=0 EndX=-70.5 EndY=-94 EndZ=0
    g11: LineSegment [constr] StartX=-70.5 StartY=-94 StartZ=0 EndX=-79.5 EndY=-94 EndZ=0
    g12: GeomPoint [constr] X=-75 Y=-95.5 Z=0
    g13: LineSegment StartX=-79.5 StartY=-94 StartZ=0 EndX=-70.5 EndY=-94 EndZ=0
    g14: LineSegment StartX=-70.5 StartY=-94 StartZ=0 EndX=-70.5 EndY=-97 EndZ=0
    g15: LineSegment StartX=-70.5 StartY=-97 StartZ=0 EndX=-73.5 EndY=-97 EndZ=0
    g16: LineSegment StartX=-73.5 StartY=-97 StartZ=0 EndX=-73.5 EndY=-100 EndZ=0
    g17: LineSegment StartX=-73.5 StartY=-100 StartZ=0 EndX=-76.5 EndY=-100 EndZ=0
    g18: LineSegment StartX=-76.5 StartY=-100 StartZ=0 EndX=-76.5 EndY=-97 EndZ=0
    g19: LineSegment StartX=-76.5 StartY=-97 StartZ=0 EndX=-79.5 EndY=-97 EndZ=0
    g20: LineSegment StartX=-79.5 StartY=-97 StartZ=0 EndX=-79.5 EndY=-94 EndZ=0
  constraints (48):
    c: Coincident(g0,g-12)
    c: PointOnObject(g0,g-11)
    c: Vertical(g0)
    c: Symmetric(g0,g-12,g1)
    c: Coincident(g2,g1)
    c: Symmetric(g-11,g-11,g2)
    c: Coincident(g3,g4)
    c: Coincident(g4,g5)
    c: Coincident(g5,g6)
    c: Coincident(g6,g3)
    c: Horizontal(g3)
    c: Horizontal(g5)
    c: Vertical(g4)
    c: Vertical(g6)
    c: PointOnObject(g3,g-11)
    c: Symmetric(g3,g4,g7)
    c: PointOnObject(g7,g2)
    c: Equal(g3,g-3)
    c: Equal(g4,g-10)
    c: Coincident(g8,g9)
    c: Coincident(g9,g10)
    c: Coincident(g10,g11)
    c: Coincident(g11,g8)
    c: Vertical(g8)
    c: Vertical(g10)
    c: Horizontal(g9)
    c: Horizontal(g11)
    c: Symmetric(g8,g10,g12)
    c: Equal(g10,g4)
    c: Equal(g11,g-7)
    c: PointOnObject(g12,g2)
    c: PointOnObject(g5,g9)
    c: Coincident(g13,g8)
    c: Coincident(g13,g10)
    c: Coincident(g14,g10)
    c: Coincident(g14,g9)
    c: Coincident(g15,g9)
    c: Coincident(g15,g4)
    c: Coincident(g16,g4)
    c: Coincident(g16,g3)
    c: Coincident(g17,g3)
    c: Coincident(g17,g3)
    c: Coincident(g18,g3)
    c: Coincident(g18,g5)
    c: Coincident(g19,g5)
    c: Coincident(g19,g8)
    c: Coincident(g20,g8)
    c: Coincident(g20,g8)
FEATURE [PartDesign::Pocket] Pocket015  label="PocketJointBottom"
  BaseFeature = -> Pocket014
  Direction = (0,0,-1)
  Length = 25
  Length2 = 5
  Profile = -> Sketch014
  ReferenceAxis = -> Sketch014 [N_Axis]
  Refine = true
  SideType = 0
  Suppressed = false
  Type = 3
  Type2 = 0
  UpToFace = -> Pocket014 [Face4]
FEATURE [Sketcher::SketchObject] Sketch015  label="SketchFrontVents"
  ArcFitTolerance = 1e-06
  AttachmentSupport = -> [Pocket015]
  ExternalGeometry = -> [Pocket015]
  ExternalTypes = [0,0,0,0,0,0,0,0]
  FullyConstrained = true
  MakeInternals = false
  MapMode = 5
  Placement = pos=(0,-10,0) rot=(1,0,0;1.5708rad)
  sketch-geometry (12):
    g0: GeomPoint X=-95.75 Y=-16 Z=0
    g1: GeomPoint [constr] X=-54.25 Y=-16 Z=0
    g2: LineSegment StartX=-111 StartY=-28 StartZ=0 EndX=-80.5 EndY=-28 EndZ=0
    g3: LineSegment StartX=-80.5 StartY=-28 StartZ=0 EndX=-80.5 EndY=-4 EndZ=0
    g4: LineSegment StartX=-80.5 StartY=-4 StartZ=0 EndX=-111 EndY=-4 EndZ=0
    g5: LineSegment StartX=-111 StartY=-4 StartZ=0 EndX=-111 EndY=-28 EndZ=0
    g6: GeomPoint [constr] X=-95.75 Y=-16 Z=0
    g7: LineSegment StartX=-69.5 StartY=-28 StartZ=0 EndX=-39 EndY=-28 EndZ=0
    g8: LineSegment StartX=-39 StartY=-28 StartZ=0 EndX=-39 EndY=-4 EndZ=0
    g9: LineSegment StartX=-39 StartY=-4 StartZ=0 EndX=-69.5 EndY=-4 EndZ=0
    g10: LineSegment StartX=-69.5 StartY=-4 StartZ=0 EndX=-69.5 EndY=-28 EndZ=0
    g11: GeomPoint [constr] X=-54.25 Y=-16 Z=0
  constraints (26):
    c: Coincident(g2,g3)
    c: Coincident(g3,g4)
    c: Coincident(g4,g5)
    c: Coincident(g5,g2)
    c: Horizontal(g2)
    c: Horizontal(g4)
    c: Vertical(g3)
    c: Vertical(g5)
    c: Symmetric(g4,g2,g6)
    c: Coincident(g7,g8)
    c: Coincident(g8,g9)
    c: Coincident(g9,g10)
    c: Coincident(g10,g7)
    c: Horizontal(g7)
    c: Horizontal(g9)
    c: Vertical(g8)
    c: Vertical(g10)
    c: Symmetric(g9,g7,g11)
    c: Distance(g4,g-4) = 4
    c: Equal(g9,g4)
    c: Equal(g10,g3)
    c: Coincident(g0,g6)
    c: Symmetric(g-8,g-5,g1)
    c: Coincident(g11,g1)
    c: Symmetric(g-6,g-10,g0)
    c: Distance(g-10,g5) = 4
FEATURE [PartDesign::Pocket] Pocket016  label="PocketFrontVents"
  BaseFeature = -> Pocket015
  Direction = (0,1,-2e-16)
  Length = 7
  Length2 = 5
  Profile = -> Sketch015
  ReferenceAxis = -> Sketch015 [N_Axis]
  Refine = true
  SideType = 1
  Suppressed = false
  Type = 3
  Type2 = 3
  UpToFace = -> Pocket015 [Face1]
  UpToFace2 = -> Pocket015 [Face22]
FEATURE [Sketcher::SketchObject] Sketch016  label="SketchSideVents"
  ArcFitTolerance = 1e-06
  AttachmentSupport = -> [Pocket016]
  ExternalGeometry = -> [Pocket016]
  ExternalTypes = [0,0,0,0]
  FullyConstrained = true
  MakeInternals = false
  MapMode = 5
  Placement = pos=(-125,0,0) rot=(0.57735,-0.57735,-0.57735;2.0944rad)
  sketch-geometry (6):
    g0: GeomPoint [constr] X=50 Y=-16 Z=0
    g1: LineSegment StartX=14 StartY=-28 StartZ=0 EndX=86 EndY=-28 EndZ=0
    g2: LineSegment StartX=86 StartY=-28 StartZ=0 EndX=86 EndY=-4 EndZ=0
    g3: LineSegment StartX=86 StartY=-4 StartZ=0 EndX=14 EndY=-4 EndZ=0
    g4: LineSegment StartX=14 StartY=-4 StartZ=0 EndX=14 EndY=-28 EndZ=0
    g5: GeomPoint [constr] X=50 Y=-16 Z=0
  constraints (13):
    c: Symmetric(g-6,g-5,g0)
    c: Coincident(g1,g2)
    c: Coincident(g2,g3)
    c: Coincident(g3,g4)
    c: Coincident(g4,g1)
    c: Horizontal(g1)
    c: Horizontal(g3)
    c: Vertical(g2)
    c: Vertical(g4)
    c: Symmetric(g3,g1,g5)
    c: Coincident(g5,g0)
    c: Distance(g-3,g4) = 4
    c: Distance(g3,g-5) = 4
FEATURE [PartDesign::Pocket] Pocket017  label="PocketSideVents001"
  BaseFeature = -> Pocket016
  Direction = (1,0,0)
  Length = 5
  Length2 = 5
  Profile = -> Sketch016
  ReferenceAxis = -> Sketch016 [N_Axis]
  Refine = true
  SideType = 0
  Suppressed = false
  Type = 3
  Type2 = 0
  UpToFace = -> Pocket016 [Face17]
FEATURE [PartDesign::Fillet] Fillet002
  Base = -> Pocket017 [Edge1,Edge2,?Edge3,Edge4,Edge5,Edge6,Edge7,Edge8,Edge9,Edge10,Edge11,Edge12,Edge13,Edge14,Edge15,Edge16,Edge17,Edge18,Edge19,Edge20,Edge21,Edge22,Edge23,Edge24,Edge25,Edge26,Edge27,Edge28,Edge29,Edge30,Edge31,Edge32,Edge33,Edge34,Edge35,Edge36,Edge37,Edge38,Edge39,Edge40,+116 more]
  BaseFeature = -> Pocket017
  Radius = 1
  Refine = true
  SupportTransform = false
  Suppressed = false
  UseAllEdges = true
FEATURE [PartDesign::Body] Body003  label="Fan Bottom"
  AllowCompound = true
  Group = -> [Binder008,Sketch012,Pad005,Hole004,Sketch013,Pocket014,Sketch014,Pocket015,Sketch015,Pocket016,Sketch016,Pocket017,Fillet002]
  Origin = -> Origin008
  Placement = pos=(0,0,-3) rot=(0,0,1;0rad)
  Tip = -> Fillet002
COMPONENT P9 — same part as P2; its construction recipe is shown at P2.
COMPONENT P10 — recipe-attached ("Pole35mm", modeled in this document).
Construction recipe (the document's own serialized feature program — sketch geometry with constraints, then the solid features built on it; lengths are millimeters unless a unit is written):

FEATURE [PartDesign::SubShapeBinder] Binder009
  BindCopyOnChange = 0
  BindMode = 0
  ClaimChildren = false
  Context = -> Body004 [Binder009.]
  Fuse = false
  MakeFace = true
  OffsetFill = false
  OffsetIntersection = false
  OffsetJoinType = 0
  OffsetOpenResult = false
  PartialLoad = false
  Refine = true
  Relative = true
  Support = -> [Sketch]
  _Version = 2
FEATURE [Sketcher::SketchObject] Sketch017
  ArcFitTolerance = 1e-06
  AttachmentSupport = -> [Origin010]
  ExternalGeometry = -> [Binder009]
  ExternalTypes = [0,0,0,0,0,0,0,0,0,0,0,0]
  FullyConstrained = true
  MakeInternals = false
  MapMode = 5
  sketch-geometry (1):
    g0: LineSegment StartX=25 StartY=100 StartZ=0 EndX=25 EndY=50 EndZ=0
  constraints (2):
    c: Coincident(g0,g-4)
    c: Coincident(g0,g-6)
FEATURE [PartDesign::Pad] Pad006  label="PadBody002"
  Direction = (0,0,1)
  Length = 3
  Length2 = 10
  Profile = -> Sketch017
  ReferenceAxis = -> Sketch017 [N_Axis]
  Refine = true
  SideType = 0
  Suppressed = false
  Type = 0
  Type2 = 0
FEATURE [PartDesign::Hole] Hole019
  BaseFeature = -> Pad006
  BaseProfileType = 7
  CustomThreadClearance = 0
  Depth = 25
  DepthType = 0
  Diameter = 4.5
  DrillForDepth = false
  DrillPoint = 1
  DrillPointAngle = 118
  HoleCutCountersinkAngle = 90
  HoleCutCustomValues = false
  HoleCutDepth = 4
  HoleCutDiameter = 8
  HoleCutType = 2
  ModelThread = false
  Profile = -> Pad006 [Edge27,Edge33,Edge30,Edge36]
  Refine = true
  Suppressed = false
  Tapered = false
  TaperedAngle = 90
  ThreadClass = 0
  ThreadDepth = 25
  ThreadDepthType = 0
  ThreadDiameter = 4
  ThreadDirection = 0
  ThreadFit = 0
  ThreadSize = 11
  ThreadType = 1
  Threaded = false
  UseCustomThreadClearance = false
FEATURE [PartDesign::Fillet] Fillet036
  Base = -> Hole019 [Edge22,Edge23,Edge25,Edge26,Edge12,Edge15,Edge19,Edge18,Edge13,Edge14,Edge16,Edge17]
  BaseFeature = -> Hole019
  Radius = 1
  Refine = true
  SupportTransform = false
  Suppressed = false
  UseAllEdges = false
FEATURE [PartDesign::Body] Body004  label="SwitchBoxTop"
  AllowCompound = true
  Group = -> [Binder009,Sketch017,Pad006,Hole019,Fillet036]
  Origin = -> Origin010
  Tip = -> Fillet036
COMPONENT P11 — recipe-attached ("Pole65mm", modeled in this document).
Construction recipe (the document's own serialized feature program — sketch geometry with constraints, then the solid features built on it; lengths are millimeters unless a unit is written):

FEATURE [PartDesign::SubShapeBinder] Binder010
  BindCopyOnChange = 0
  BindMode = 0
  ClaimChildren = false
  Context = -> Body005 [Binder010.]
  Fuse = false
  MakeFace = true
  OffsetFill = false
  OffsetIntersection = false
  OffsetJoinType = 0
  OffsetOpenResult = false
  PartialLoad = false
  Refine = true
  Relative = true
  Support = -> [Sketch]
  _Version = 2
FEATURE [Sketcher::SketchObject] Sketch018  label="SketchBody"
  ArcFitTolerance = 1e-06
  AttachmentSupport = -> [Origin012]
  ExternalGeometry = -> [Binder010]
  ExternalTypes = [0,0,0,0,0,0,0,0]
  FullyConstrained = true
  MakeInternals = false
  MapMode = 5
  sketch-geometry (40):
    g0: LineSegment [constr] StartX=35 StartY=90 StartZ=0 EndX=35 EndY=100 EndZ=0
    g1: LineSegment [constr] StartX=35 StartY=100 StartZ=0 EndX=25 EndY=100 EndZ=0
    g2: LineSegment [constr] StartX=25 StartY=100 StartZ=0 EndX=25 EndY=90 EndZ=0
    g3: LineSegment [constr] StartX=25 StartY=90 StartZ=0 EndX=35 EndY=90 EndZ=0
    g4: GeomPoint [constr] X=30 Y=95 Z=0
    g5: LineSegment [constr] StartX=115 StartY=90 StartZ=0 EndX=125 EndY=90 EndZ=0
    g6: LineSegment [constr] StartX=125 StartY=90 StartZ=0 EndX=125 EndY=100 EndZ=0
    g7: LineSegment [constr] StartX=125 StartY=100 StartZ=0 EndX=115 EndY=100 EndZ=0
    g8: LineSegment [constr] StartX=115 StartY=100 StartZ=0 EndX=115 EndY=90 EndZ=0
    g9: GeomPoint [constr] X=120 Y=95 Z=0
    g10: LineSegment [constr] StartX=115 StartY=60 StartZ=0 EndX=115 EndY=50 EndZ=0
    g11: LineSegment [constr] StartX=115 StartY=50 StartZ=0 EndX=125 EndY=50 EndZ=0
    g12: LineSegment [constr] StartX=125 StartY=50 StartZ=0 EndX=125 EndY=60 EndZ=0
    g13: LineSegment [constr] StartX=125 StartY=60 StartZ=0 EndX=115 EndY=60 EndZ=0
    g14: GeomPoint [constr] X=120 Y=55 Z=0
    g15: LineSegment [constr] StartX=35 StartY=60 StartZ=0 EndX=25 EndY=60 EndZ=0
    g16: LineSegment [constr] StartX=25 StartY=60 StartZ=0 EndX=25 EndY=50 EndZ=0
    g17: LineSegment [constr] StartX=25 StartY=50 StartZ=0 EndX=35 EndY=50 EndZ=0
    g18: LineSegment [constr] StartX=35 StartY=50 StartZ=0 EndX=35 EndY=60 EndZ=0
    g19: GeomPoint [constr] X=30 Y=55 Z=0
    g20: LineSegment [constr] StartX=28 StartY=90 StartZ=0 EndX=28 EndY=60 EndZ=0
    g21: LineSegment [constr] StartX=115 StartY=58 StartZ=0 EndX=35 EndY=58 EndZ=0
    g22: LineSegment [constr] StartX=35 StartY=92 StartZ=0 EndX=115 EndY=92 EndZ=0
    g23: LineSegment StartX=25 StartY=100 StartZ=0 EndX=25 EndY=50 EndZ=0
    g24: LineSegment StartX=25 StartY=50 StartZ=0 EndX=125 EndY=50 EndZ=0
    g25: LineSegment StartX=125 StartY=50 StartZ=0 EndX=125 EndY=100 EndZ=0
    g26: LineSegment StartX=125 StartY=100 StartZ=0 EndX=25 EndY=100 EndZ=0
    g27: LineSegment StartX=35 StartY=92 StartZ=0 EndX=35 EndY=90 EndZ=0
    g28: LineSegment StartX=35 StartY=90 StartZ=0 EndX=28 EndY=90 EndZ=0
    g29: LineSegment StartX=28 StartY=90 StartZ=0 EndX=28 EndY=60 EndZ=0
    g30: LineSegment StartX=28 StartY=60 StartZ=0 EndX=35 EndY=60 EndZ=0
    g31: LineSegment StartX=35 StartY=60 StartZ=0 EndX=35 EndY=58 EndZ=0
    g32: LineSegment StartX=35 StartY=58 StartZ=0 EndX=115 EndY=58 EndZ=0
    g33: LineSegment StartX=115 StartY=58 StartZ=0 EndX=115 EndY=60 EndZ=0
    g34: LineSegment StartX=35 StartY=92 StartZ=0 EndX=115 EndY=92 EndZ=0
    g35: LineSegment StartX=115 StartY=92 StartZ=0 EndX=115 EndY=90 EndZ=0
    g36: LineSegment [constr] StartX=122 StartY=60 StartZ=0 EndX=122 EndY=90 EndZ=0
    g37: LineSegment StartX=115 StartY=90 StartZ=0 EndX=122 EndY=90 EndZ=0
    g38: LineSegment StartX=122 StartY=90 StartZ=0 EndX=122 EndY=60 EndZ=0
    g39: LineSegment StartX=122 StartY=60 StartZ=0 EndX=115 EndY=60 EndZ=0
  constraints (92):
    c: Coincident(g0,g1)
    c: Coincident(g1,g2)
    c: Coincident(g2,g3)
    c: Coincident(g3,g0)
    c: Vertical(g0)
    c: Vertical(g2)
    c: Horizontal(g1)
    c: Horizontal(g3)
    c: Symmetric(g2,g0,g4)
    c: Coincident(g4,g-7)
    c: Coincident(g1,g-4)
    c: Coincident(g5,g6)
    c: Coincident(g6,g7)
    c: Coincident(g7,g8)
    c: Coincident(g8,g5)
    c: Horizontal(g5)
    c: Horizontal(g7)
    c: Vertical(g6)
    c: Vertical(g8)
    c: Symmetric(g7,g5,g9)
    c: Coincident(g9,g-10)
    c: Coincident(g6,g-6)
    c: Coincident(g10,g11)
    c: Coincident(g11,g12)
    c: Coincident(g12,g13)
    c: Coincident(g13,g10)
    c: Vertical(g10)
    c: Vertical(g12)
    c: Horizontal(g11)
    c: Horizontal(g13)
    c: Symmetric(g12,g10,g14)
    c: Coincident(g14,g-9)
    c: Coincident(g11,g-6)
    c: Coincident(g15,g16)
    c: Coincident(g16,g17)
    c: Coincident(g17,g18)
    c: Coincident(g18,g15)
    c: Horizontal(g15)
    c: Horizontal(g17)
    c: Vertical(g16)
    c: Vertical(g18)
    c: Symmetric(g17,g15,g19)
    c: Coincident(g19,g-8)
    c: Coincident(g16,g-5)
    c: PointOnObject(g20,g3)
    c: PointOnObject(g20,g15)
    c: Vertical(g20)
    c: PointOnObject(g21,g10)
    c: PointOnObject(g21,g18)
    c: Horizontal(g21)
    c: Distance(g-5,g21) = 8
    c: Distance(g20,g-3) = 3
    c: PointOnObject(g22,g0)
    c: PointOnObject(g22,g8)
    c: Horizontal(g22)
    c: Distance(g-4,g22) = 8
    c: Coincident(g23,g1)
    c: Coincident(g23,g16)
    c: Coincident(g24,g16)
    c: Coincident(g24,g11)
    c: Coincident(g25,g11)
    c: Coincident(g25,g6)
    c: Coincident(g26,g6)
    c: Coincident(g26,g1)
    c: Coincident(g27,g22)
    c: Coincident(g27,g0)
    c: Coincident(g28,g0)
    c: Coincident(g28,g20)
    c: Coincident(g29,g20)
    c: Coincident(g29,g20)
    c: Coincident(g30,g20)
    c: Coincident(g30,g15)
    c: Coincident(g31,g15)
    c: Coincident(g31,g21)
    c: Coincident(g32,g21)
    c: Coincident(g32,g21)
    c: Coincident(g33,g21)
    c: Coincident(g33,g10)
    c: Coincident(g34,g22)
    c: Coincident(g34,g22)
    c: Coincident(g35,g22)
    c: Coincident(g35,g5)
    c: Vertical(g36)
    c: PointOnObject(g36,g5)
    c: PointOnObject(g36,g13)
    c: Distance(g25,g36) = 3
    c: Coincident(g37,g5)
    c: Coincident(g37,g36)
    c: Coincident(g38,g36)
    c: Coincident(g38,g36)
    c: Coincident(g39,g36)
    c: Coincident(g39,g10)
FEATURE [PartDesign::Pad] Pad007  label="PadBody003"
  Direction = (0,0,1)
  Length = 32
  Length2 = 10
  Profile = -> Sketch018
  ReferenceAxis = -> Sketch018 [N_Axis]
  Refine = true
  SideType = 0
  Suppressed = false
  Type = 0
  Type2 = 0
FEATURE [Sketcher::SketchObject] Sketch019  label="SketchHoles001"
  ArcFitTolerance = 1e-06
  AttachmentSupport = -> [Pad007]
  ExternalGeometry = -> [Binder010]
  ExternalTypes = [0,0,0,0]
  FullyConstrained = true
  MakeInternals = false
  MapMode = 5
  Placement = pos=(0,0,32) rot=(0,0,1;0rad)
FEATURE [PartDesign::Hole] Hole006  label="HoleScrews002"
  BaseFeature = -> Pad007
  BaseProfileType = 7
  CustomThreadClearance = 0
  Depth = 35
  DepthType = 0
  Diameter = 3.7
  DrillForDepth = false
  DrillPoint = 1
  DrillPointAngle = 118
  HoleCutCountersinkAngle = 90
  HoleCutCustomValues = false
  HoleCutDepth = 0
  HoleCutDiameter = 0
  HoleCutType = 0
  ModelThread = false
  Profile = -> Sketch019
  Refine = true
  Suppressed = false
  Tapered = false
  TaperedAngle = 90
  ThreadClass = 0
  ThreadDepth = 35
  ThreadDepthType = 0
  ThreadDiameter = 4.5
  ThreadDirection = 0
  ThreadFit = 0
  ThreadSize = 12
  ThreadType = 1
  Threaded = true
  UseCustomThreadClearance = false
FEATURE [Sketcher::SketchObject] Sketch020  label="SketchJoints"
  ArcFitTolerance = 1e-06
  AttachmentSupport = -> [Hole006]
  ExternalGeometry = -> [Binder010]
  ExternalTypes = [0,0,0]
  FullyConstrained = true
  MakeInternals = false
  MapMode = 5
  Placement = pos=(0,0,32) rot=(0,0,1;0rad)
  sketch-geometry (55):
    g0: LineSegment [constr] StartX=25 StartY=100 StartZ=0 EndX=25 EndY=90 EndZ=0
    g1: LineSegment [constr] StartX=25 StartY=90 StartZ=0 EndX=125 EndY=90 EndZ=0
    g2: LineSegment [constr] StartX=125 StartY=90 StartZ=0 EndX=125 EndY=100 EndZ=0
    g3: LineSegment [constr] StartX=125 StartY=100 StartZ=0 EndX=25 EndY=100 EndZ=0
    g4: LineSegment [constr] StartX=25 StartY=60 StartZ=0 EndX=25 EndY=50 EndZ=0
    g5: LineSegment [constr] StartX=25 StartY=50 StartZ=0 EndX=125 EndY=50 EndZ=0
    g6: LineSegment [constr] StartX=125 StartY=50 StartZ=0 EndX=125 EndY=60 EndZ=0
    g7: LineSegment [constr] StartX=125 StartY=60 StartZ=0 EndX=25 EndY=60 EndZ=0
    g8: GeomPoint [constr] X=75 Y=95 Z=0
    g9: GeomPoint [constr] X=75 Y=55 Z=0
    g10: LineSegment [constr] StartX=75 StartY=100 StartZ=0 EndX=75 EndY=50 EndZ=0
    g11: LineSegment [constr] StartX=73.5 StartY=100 StartZ=0 EndX=73.5 EndY=97 EndZ=0
    g12: LineSegment [constr] StartX=73.5 StartY=97 StartZ=0 EndX=76.5 EndY=97 EndZ=0
    g13: LineSegment [constr] StartX=76.5 StartY=97 StartZ=0 EndX=76.5 EndY=100 EndZ=0
    g14: LineSegment [constr] StartX=76.5 StartY=100 StartZ=0 EndX=73.5 EndY=100 EndZ=0
    g15: LineSegment [constr] StartX=70.5 StartY=97 StartZ=0 EndX=70.5 EndY=94 EndZ=0
    g16: LineSegment [constr] StartX=70.5 StartY=94 StartZ=0 EndX=79.5 EndY=94 EndZ=0
    g17: LineSegment [constr] StartX=79.5 StartY=94 StartZ=0 EndX=79.5 EndY=97 EndZ=0
    g18: LineSegment [constr] StartX=79.5 StartY=97 StartZ=0 EndX=70.5 EndY=97 EndZ=0
    g19: GeomPoint [constr] X=75 Y=95.5 Z=0
    g20: GeomPoint [constr] X=75 Y=98.5 Z=0
    g21: LineSegment [constr] StartX=75 StartY=98.5 StartZ=0 EndX=75 EndY=97 EndZ=0
    g22: LineSegment [constr] StartX=75 StartY=97 StartZ=0 EndX=75 EndY=95.5 EndZ=0
    g23: GeomPoint [constr] X=75 Y=97 Z=0
    g24: LineSegment [constr] StartX=75 StartY=98.5 StartZ=0 EndX=75 EndY=100 EndZ=0
    g25: LineSegment StartX=73.5 StartY=100 StartZ=0 EndX=76.5 EndY=100 EndZ=0
    g26: LineSegment StartX=76.5 StartY=100 StartZ=0 EndX=76.5 EndY=97 EndZ=0
    g27: LineSegment StartX=76.5 StartY=97 StartZ=0 EndX=79.5 EndY=97 EndZ=0
    g28: LineSegment StartX=79.5 StartY=97 StartZ=0 EndX=79.5 EndY=94 EndZ=0
    g29: LineSegment StartX=79.5 StartY=94 StartZ=0 EndX=70.5 EndY=94 EndZ=0
    g30: LineSegment StartX=70.5 StartY=94 StartZ=0 EndX=70.5 EndY=97 EndZ=0
    g31: LineSegment StartX=70.5 StartY=97 StartZ=0 EndX=73.5 EndY=97 EndZ=0
    g32: LineSegment StartX=73.5 StartY=97 StartZ=0 EndX=73.5 EndY=100 EndZ=0
    g33: LineSegment [constr] StartX=70.5 StartY=56 StartZ=0 EndX=70.5 EndY=53 EndZ=0
    g34: LineSegment [constr] StartX=70.5 StartY=53 StartZ=0 EndX=79.5 EndY=53 EndZ=0
    g35: LineSegment [constr] StartX=79.5 StartY=53 StartZ=0 EndX=79.5 EndY=56 EndZ=0
    g36: LineSegment [constr] StartX=79.5 StartY=56 StartZ=0 EndX=70.5 EndY=56 EndZ=0
    g37: LineSegment [constr] StartX=73.5 StartY=53 StartZ=0 EndX=73.5 EndY=50 EndZ=0
    g38: LineSegment [constr] StartX=73.5 StartY=50 StartZ=0 EndX=76.5 EndY=50 EndZ=0
    g39: LineSegment [constr] StartX=76.5 StartY=50 StartZ=0 EndX=76.5 EndY=53 EndZ=0
    g40: LineSegment [constr] StartX=76.5 StartY=53 StartZ=0 EndX=73.5 EndY=53 EndZ=0
    g41: GeomPoint [constr] X=75 Y=54.5 Z=0
    g42: LineSegment [constr] StartX=75 StartY=56 StartZ=0 EndX=75 EndY=53 EndZ=0
    g43: GeomPoint [constr] X=75 Y=51.5 Z=0
    g44: LineSegment [constr] StartX=75 StartY=53 StartZ=0 EndX=75 EndY=51.5 EndZ=0
    g45: LineSegment [constr] StartX=75 StartY=51.5 StartZ=0 EndX=75 EndY=50 EndZ=0
    g46: LineSegment [constr] StartX=70.5 StartY=56 StartZ=0 EndX=79.5 EndY=56 EndZ=0
    g47: LineSegment StartX=70.5 StartY=56 StartZ=0 EndX=79.5 EndY=56 EndZ=0
    g48: LineSegment StartX=79.5 StartY=56 StartZ=0 EndX=79.5 EndY=53 EndZ=0
    g49: LineSegment StartX=79.5 StartY=53 StartZ=0 EndX=76.5 EndY=53 EndZ=0
    g50: LineSegment StartX=76.5 StartY=53 StartZ=0 EndX=76.5 EndY=50 EndZ=0
    g51: LineSegment StartX=76.5 StartY=50 StartZ=0 EndX=73.5 EndY=50 EndZ=0
    g52: LineSegment StartX=73.5 StartY=50 StartZ=0 EndX=73.5 EndY=53 EndZ=0
    g53: LineSegment StartX=73.5 StartY=53 StartZ=0 EndX=70.5 EndY=53 EndZ=0
    g54: LineSegment StartX=70.5 StartY=53 StartZ=0 EndX=70.5 EndY=56 EndZ=0
  constraints (130):
    c: Coincident(g0,g1)
    c: Coincident(g1,g2)
    c: Coincident(g2,g3)
    c: Coincident(g3,g0)
    c: Vertical(g0)
    c: Vertical(g2)
    c: Horizontal(g1)
    c: Horizontal(g3)
    c: Coincident(g0,g-4)
    c: PointOnObject(g1,g-5)
    c: Distance(g3,g1) = 10
    c: Coincident(g4,g5)
    c: Coincident(g5,g6)
    c: Coincident(g6,g7)
    c: Coincident(g7,g4)
    c: Vertical(g4)
    c: Vertical(g6)
    c: Horizontal(g5)
    c: Horizontal(g7)
    c: PointOnObject(g4,g-4)
    c: Coincident(g5,g-5)
    c: Distance(g5,g7) = 10
    c: Symmetric(g0,g2,g8)
    c: Symmetric(g4,g6,g9)
    c: Vertical(g10)
    c: PointOnObject(g10,g5)
    c: PointOnObject(g10,g3)
    c: PointOnObject(g8,g10)
    c: Coincident(g11,g12)
    c: Coincident(g12,g13)
    c: Coincident(g13,g14)
    c: Coincident(g14,g11)
    c: Vertical(g11)
    c: Vertical(g13)
    c: Horizontal(g12)
    c: Horizontal(g14)
    c: Coincident(g15,g16)
    c: Coincident(g16,g17)
    c: Coincident(g17,g18)
    c: Coincident(g18,g15)
    c: Vertical(g15)
    c: Vertical(g17)
    c: Horizontal(g16)
    c: Horizontal(g18)
    c: DistanceX(g14,g14) = 3
    c: Equal(g13,g14)
    c: Symmetric(g15,g17,g19)
    c: Symmetric(g11,g13,g20)
    c: Coincident(g21,g20)
    c: Symmetric(g18,g18,g21)
    c: Vertical(g21)
    c: Coincident(g22,g21)
    c: Coincident(g22,g19)
    c: PointOnObject(g23,g12)
    c: PointOnObject(g23,g21)
    c: PointOnObject(g23,g18)
    c: DistanceX(g18,g18) = 9
    c: Equal(g17,g13)
    c: Coincident(g24,g20)
    c: Symmetric(g14,g14,g24)
    c: Coincident(g24,g10)
    c: Coincident(g25,g11)
    c: Coincident(g25,g13)
    c: Coincident(g26,g13)
    c: Coincident(g26,g12)
    c: Coincident(g27,g12)
    c: Coincident(g27,g17)
    c: Coincident(g28,g17)
    c: Coincident(g28,g16)
    c: Coincident(g29,g16)
    c: Coincident(g29,g15)
    c: Coincident(g30,g15)
    c: Coincident(g30,g15)
    c: Coincident(g31,g15)
    c: Coincident(g31,g11)
    c: Coincident(g32,g11)
    c: Coincident(g32,g11)
    c: Coincident(g33,g34)
    c: Coincident(g34,g35)
    c: Coincident(g35,g36)
    c: Coincident(g36,g33)
    c: Vertical(g33)
    c: Vertical(g35)
    c: Horizontal(g34)
    c: Horizontal(g36)
    c: Coincident(g37,g38)
    c: Coincident(g38,g39)
    c: Coincident(g39,g40)
    c: Coincident(g40,g37)
    c: Vertical(g37)
    c: Vertical(g39)
    c: Horizontal(g38)
    c: Horizontal(g40)
    c: PointOnObject(g37,g34)
    c: Equal(g38,g37)
    c: Equal(g37,g25)
    c: Equal(g39,g35)
    c: Equal(g34,g29)
    c: Symmetric(g33,g35,g41)
    c: Vertical(g42)
    c: PointOnObject(g41,g42)
    c: PointOnObject(g42,g34)
    c: PointOnObject(g42,g36)
    c: Symmetric(g37,g39,g43)
    c: Vertical(g44)
    c: Coincident(g44,g42)
    c: Coincident(g44,g43)
    c: PointOnObject(g45,g38)
    c: Vertical(g45)
    c: Coincident(g45,g43)
    c: Coincident(g45,g10)
    c: Coincident(g47,g46)
    c: Coincident(g47,g46)
    c: Horizontal(g47)
    c: Coincident(g46,g33)
    c: Equal(g47,g36)
    c: Coincident(g48,g35)
    c: Coincident(g48,g34)
    c: Coincident(g49,g34)
    c: Coincident(g49,g39)
    c: Coincident(g50,g39)
    c: Coincident(g50,g38)
    c: Coincident(g51,g38)
    c: Coincident(g51,g37)
    c: Coincident(g52,g37)
    c: Coincident(g52,g37)
    c: Coincident(g53,g37)
    c: Coincident(g53,g33)
    c: Coincident(g54,g33)
    c: Coincident(g54,g33)
FEATURE [PartDesign::Pocket] Pocket018  label="PocketJoints"
  BaseFeature = -> Hole006
  Direction = (0,0,-1)
  Length = 5
  Length2 = 5
  Profile = -> Sketch020
  ReferenceAxis = -> Sketch020 [N_Axis]
  Refine = true
  SideType = 0
  Suppressed = false
  Type = 3
  Type2 = 0
  UpToFace = -> Hole006 [Face4]
FEATURE [Sketcher::SketchObject] Sketch021  label="SketchFrontVents001"
  ArcFitTolerance = 1e-06
  AttachmentSupport = -> [Pocket018]
  ExternalGeometry = -> [Pocket018]
  ExternalTypes = [0,0,0,0,0,0,0,0]
  FullyConstrained = true
  MakeInternals = false
  MapMode = 5
  Placement = pos=(0,50,0) rot=(1,0,0;1.5708rad)
  sketch-geometry (12):
    g0: GeomPoint [constr] X=54.25 Y=16 Z=0
    g1: GeomPoint [constr] X=95.75 Y=16 Z=0
    g2: LineSegment StartX=40 StartY=5 StartZ=0 EndX=68.5 EndY=5 EndZ=0
    g3: LineSegment StartX=68.5 StartY=5 StartZ=0 EndX=68.5 EndY=27 EndZ=0
    g4: LineSegment StartX=68.5 StartY=27 StartZ=0 EndX=40 EndY=27 EndZ=0
    g5: LineSegment StartX=40 StartY=27 StartZ=0 EndX=40 EndY=5 EndZ=0
    g6: GeomPoint [constr] X=54.25 Y=16 Z=0
    g7: LineSegment StartX=81.5 StartY=5 StartZ=0 EndX=110 EndY=5 EndZ=0
    g8: LineSegment StartX=110 StartY=5 StartZ=0 EndX=110 EndY=27 EndZ=0
    g9: LineSegment StartX=110 StartY=27 StartZ=0 EndX=81.5 EndY=27 EndZ=0
    g10: LineSegment StartX=81.5 StartY=27 StartZ=0 EndX=81.5 EndY=5 EndZ=0
    g11: GeomPoint [constr] X=95.75 Y=16 Z=0
  constraints (26):
    c: Symmetric(g-3,g-7,g0)
    c: Symmetric(g-10,g-4,g1)
    c: Coincident(g2,g3)
    c: Coincident(g3,g4)
    c: Coincident(g4,g5)
    c: Coincident(g5,g2)
    c: Horizontal(g2)
    c: Horizontal(g4)
    c: Vertical(g3)
    c: Vertical(g5)
    c: Symmetric(g4,g2,g6)
    c: Coincident(g6,g0)
    c: Coincident(g7,g8)
    c: Coincident(g8,g9)
    c: Coincident(g9,g10)
    c: Coincident(g10,g7)
    c: Horizontal(g7)
    c: Horizontal(g9)
    c: Vertical(g8)
    c: Vertical(g10)
    c: Symmetric(g9,g7,g11)
    c: Coincident(g11,g1)
    c: Distance(g-6,g4) = 5
    c: Distance(g-3,g5) = 5
    c: Equal(g9,g4)
    c: Equal(g10,g3)
FEATURE [PartDesign::Pocket] Pocket019  label="PocketFrontVents001"
  BaseFeature = -> Pocket018
  Direction = (0,1,-2e-16)
  Length = 5
  Length2 = 5
  Profile = -> Sketch021
  ReferenceAxis = -> Sketch021 [N_Axis]
  Refine = true
  SideType = 0
  Suppressed = false
  Type = 3
  Type2 = 0
  UpToFace = -> Pocket018 [Face14]
FEATURE [Sketcher::SketchObject] Sketch022  label="SketchSideVents001"
  ArcFitTolerance = 1e-06
  AttachmentSupport = -> [Pocket019]
  ExternalGeometry = -> [Pocket019]
  ExternalTypes = [0,0,0,0]
  FullyConstrained = true
  MakeInternals = false
  MapMode = 5
  Placement = pos=(25,0,0) rot=(0.57735,-0.57735,-0.57735;2.0944rad)
  sketch-geometry (6):
    g0: GeomPoint [constr] X=-75 Y=16 Z=0
    g1: LineSegment StartX=-85 StartY=5 StartZ=0 EndX=-65 EndY=5 EndZ=0
    g2: LineSegment StartX=-65 StartY=5 StartZ=0 EndX=-65 EndY=27 EndZ=0
    g3: LineSegment StartX=-65 StartY=27 StartZ=0 EndX=-85 EndY=27 EndZ=0
    g4: LineSegment StartX=-85 StartY=27 StartZ=0 EndX=-85 EndY=5 EndZ=0
    g5: GeomPoint [constr] X=-75 Y=16 Z=0
  constraints (13):
    c: Symmetric(g-3,g-5,g0)
    c: Coincident(g1,g2)
    c: Coincident(g2,g3)
    c: Coincident(g3,g4)
    c: Coincident(g4,g1)
    c: Horizontal(g1)
    c: Horizontal(g3)
    c: Vertical(g2)
    c: Vertical(g4)
    c: Symmetric(g3,g1,g5)
    c: Coincident(g5,g0)
    c: Distance(g-5,g3) = 5
    c: Distance(g-4,g2) = 5
FEATURE [PartDesign::Pocket] Pocket020  label="PocketSideVents002"
  BaseFeature = -> Pocket019
  Direction = (1,0,0)
  Length = 5
  Length2 = 5
  Profile = -> Sketch022
  ReferenceAxis = -> Sketch022 [N_Axis]
  Refine = true
  SideType = 0
  Suppressed = false
  Type = 3
  Type2 = 0
  UpToFace = -> Pocket019 [Face23]
FEATURE [PartDesign::Fillet] Fillet004
  Base = -> Pocket020 [Face61,Face62,Face60,Face59,Face48,Face49,Face50,Face47,Face14,Face13,Face11,Face54,Face51,Face53,Face52,Face12]
  BaseFeature = -> Pocket020
  Radius = 1
  Refine = true
  SupportTransform = false
  Suppressed = false
  UseAllEdges = false
FEATURE [PartDesign::Fillet] Fillet005
  Base = -> Fillet004 [Face75,Face78,Edge138,Face76,Face77,Face58,Face55,Face57,Face56]
  BaseFeature = -> Fillet004
  Radius = 1
  Refine = true
  SupportTransform = false
  Suppressed = false
  UseAllEdges = false
FEATURE [PartDesign::Fillet] Fillet006
  Base = -> Fillet005 [Face10,Face37,Face1,Face13,Face39,Face38]
  BaseFeature = -> Fillet005
  Radius = 1
  Refine = true
  SupportTransform = false
  Suppressed = false
  UseAllEdges = false
FEATURE [PartDesign::Fillet] Fillet007
  Base = -> Fillet006 [Edge87,Edge78,Edge80,Edge82,Edge84,Edge86,Edge88,Edge85,Edge83,Edge81,Edge79,Edge77]
  BaseFeature = -> Fillet006
  Radius = 1
  Refine = true
  SupportTransform = false
  Suppressed = false
  UseAllEdges = false
FEATURE [PartDesign::Fillet] Fillet008
  Base = -> Fillet007 [Vertex81,Edge141,Edge145,Edge165,Edge169,Edge172,Edge171,Edge167,Edge155,Edge143,Edge138,Edge118]
  BaseFeature = -> Fillet007
  Radius = 1
  Refine = true
  SupportTransform = false
  Suppressed = false
  UseAllEdges = false
FEATURE [PartDesign::Fillet] Fillet009
  Base = -> Fillet008 [Edge143,Edge272,Edge178,Edge67]
  BaseFeature = -> Fillet008
  Radius = 1
  Refine = true
  SupportTransform = false
  Suppressed = false
  UseAllEdges = false
FEATURE [PartDesign::Fillet] Fillet010
  Base = -> Fillet009 [Edge162,Edge160,Edge164,Edge168,Edge172,Edge158]
  BaseFeature = -> Fillet009
  Radius = 1
  Refine = true
  SupportTransform = false
  Suppressed = false
  UseAllEdges = false
FEATURE [PartDesign::Body] Body005  label="SwitchBoxBottom"
  AllowCompound = true
  Group = -> [Binder010,Sketch018,Pad007,Sketch019,Hole006,Sketch020,Pocket018,Sketch021,Pocket019,Sketch022,Pocket020,Fillet004,Fillet005,Fillet006,Fillet007,Fillet008,Fillet009,Fillet010]
  Origin = -> Origin012
  Tip = -> Fillet010
COMPONENT P12 — same part as P8; its construction recipe is shown at P8.
COMPONENT P13 — same part as P8; its construction recipe is shown at P8.
COMPONENT P14 — same part as P8; its construction recipe is shown at P8.
COMPONENT P15 — same part as P8; its construction recipe is shown at P8.
COMPONENT P16 — same part as P8; its construction recipe is shown at P8.
COMPONENT P17 — recipe-attached ("RaspberryPiBottom001", modeled in this document).
Construction recipe (the document's own serialized feature program — sketch geometry with constraints, then the solid features built on it; lengths are millimeters unless a unit is written):

FEATURE [Sketcher::SketchObject] Sketch052
  ArcFitTolerance = 1e-06
  AttachmentSupport = -> [Origin032]
  ExternalTypes = [0]
  FullyConstrained = true
  MakeInternals = false
  MapMode = 5
  sketch-geometry (50):
    g0: LineSegment StartX=-50 StartY=-25 StartZ=0 EndX=50 EndY=-25 EndZ=0
    g1: LineSegment StartX=50 StartY=-25 StartZ=0 EndX=50 EndY=25 EndZ=0
    g2: LineSegment StartX=50 StartY=25 StartZ=0 EndX=-50 EndY=25 EndZ=0
    g3: LineSegment StartX=-50 StartY=25 StartZ=0 EndX=-50 EndY=-25 EndZ=0
    g4: GeomPoint [constr] X=0 Y=0 Z=0
    g5: LineSegment [constr] StartX=-45 StartY=-20 StartZ=0 EndX=45 EndY=-20 EndZ=0
    g6: LineSegment [constr] StartX=45 StartY=-20 StartZ=0 EndX=45 EndY=20 EndZ=0
    g7: LineSegment [constr] StartX=45 StartY=20 StartZ=0 EndX=-45 EndY=20 EndZ=0
    g8: LineSegment [constr] StartX=-45 StartY=20 StartZ=0 EndX=-45 EndY=-20 EndZ=0
    g9: GeomPoint [constr] X=0 Y=0 Z=0
    g10: Circle CenterX=45 CenterY=20 CenterZ=0 NormalX=0 NormalY=0 NormalZ=1 AngleXU=0 Radius=2
    g11: Circle CenterX=45 CenterY=-20 CenterZ=0 NormalX=0 NormalY=0 NormalZ=1 AngleXU=0 Radius=2
    g12: Circle CenterX=-45 CenterY=-20 CenterZ=0 NormalX=0 NormalY=0 NormalZ=1 AngleXU=0 Radius=2
    g13: Circle CenterX=-45 CenterY=20 CenterZ=0 NormalX=0 NormalY=0 NormalZ=1 AngleXU=0 Radius=2
    g14: GeomPoint [constr] X=0 Y=25 Z=0
    g15: GeomPoint [constr] X=0 Y=-25 Z=0
    g16: LineSegment [constr] StartX=-1.5 StartY=-22 StartZ=0 EndX=-1.5 EndY=-25 EndZ=0
    g17: LineSegment [constr] StartX=-1.5 StartY=-25 StartZ=0 EndX=1.5 EndY=-25 EndZ=0
    g18: LineSegment [constr] StartX=1.5 StartY=-25 StartZ=0 EndX=1.5 EndY=-22 EndZ=0
    g19: LineSegment [constr] StartX=1.5 StartY=-22 StartZ=0 EndX=-1.5 EndY=-22 EndZ=0
    g20: LineSegment [constr] StartX=-4.5 StartY=-19 StartZ=0 EndX=-4.5 EndY=-22 EndZ=0
    g21: LineSegment [constr] StartX=-4.5 StartY=-22 StartZ=0 EndX=4.5 EndY=-22 EndZ=0
    g22: LineSegment [constr] StartX=4.5 StartY=-22 StartZ=0 EndX=4.5 EndY=-19 EndZ=0
    g23: LineSegment [constr] StartX=4.5 StartY=-19 StartZ=0 EndX=-4.5 EndY=-19 EndZ=0
    g24: GeomPoint [constr] X=0 Y=-22 Z=0
    g25: LineSegment [constr] StartX=-1.5 StartY=25 StartZ=0 EndX=-1.5 EndY=22 EndZ=0
    g26: LineSegment [constr] StartX=-1.5 StartY=22 StartZ=0 EndX=1.5 EndY=22 EndZ=0
    g27: LineSegment [constr] StartX=1.5 StartY=22 StartZ=0 EndX=1.5 EndY=25 EndZ=0
    g28: LineSegment [constr] StartX=1.5 StartY=25 StartZ=0 EndX=-1.5 EndY=25 EndZ=0
    g29: LineSegment [constr] StartX=-4.5 StartY=22 StartZ=0 EndX=-4.5 EndY=19 EndZ=0
    g30: LineSegment [constr] StartX=-4.5 StartY=19 StartZ=0 EndX=4.5 EndY=19 EndZ=0
    g31: LineSegment [constr] StartX=4.5 StartY=19 StartZ=0 EndX=4.5 EndY=22 EndZ=0
    g32: LineSegment [constr] StartX=4.5 StartY=22 StartZ=0 EndX=-4.5 EndY=22 EndZ=0
    g33: GeomPoint [constr] X=0 Y=22 Z=0
    g34: LineSegment StartX=-1.5 StartY=25 StartZ=0 EndX=1.5 EndY=25 EndZ=0
    g35: LineSegment StartX=1.5 StartY=25 StartZ=0 EndX=1.5 EndY=22 EndZ=0
    g36: LineSegment StartX=1.5 StartY=22 StartZ=0 EndX=4.5 EndY=22 EndZ=0
    g37: LineSegment StartX=4.5 StartY=22 StartZ=0 EndX=4.5 EndY=19 EndZ=0
    g38: LineSegment StartX=4.5 StartY=19 StartZ=0 EndX=-4.5 EndY=19 EndZ=0
    g39: LineSegment StartX=-4.5 StartY=19 StartZ=0 EndX=-4.5 EndY=22 EndZ=0
    g40: LineSegment StartX=-4.5 StartY=22 StartZ=0 EndX=-1.5 EndY=22 EndZ=0
    g41: LineSegment StartX=-1.5 StartY=22 StartZ=0 EndX=-1.5 EndY=25 EndZ=0
    g42: LineSegment StartX=-4.5 StartY=-19 StartZ=0 EndX=4.5 EndY=-19 EndZ=0
    g43: LineSegment StartX=4.5 StartY=-19 StartZ=0 EndX=4.5 EndY=-22 EndZ=0
    g44: LineSegment StartX=4.5 StartY=-22 StartZ=0 EndX=1.5 EndY=-22 EndZ=0
    g45: LineSegment StartX=1.5 StartY=-22 StartZ=0 EndX=1.5 EndY=-25 EndZ=0
    g46: LineSegment StartX=1.5 StartY=-25 StartZ=0 EndX=-1.5 EndY=-25 EndZ=0
    g47: LineSegment StartX=-1.5 StartY=-25 StartZ=0 EndX=-1.5 EndY=-22 EndZ=0
    g48: LineSegment StartX=-1.5 StartY=-22 StartZ=0 EndX=-4.5 EndY=-22 EndZ=0
    g49: LineSegment StartX=-4.5 StartY=-22 StartZ=0 EndX=-4.5 EndY=-19 EndZ=0
  constraints (114):
    c: Coincident(g0,g1)
    c: Coincident(g1,g2)
    c: Coincident(g2,g3)
    c: Coincident(g3,g0)
    c: Horizontal(g0)
    c: Horizontal(g2)
    c: Vertical(g1)
    c: Vertical(g3)
    c: Symmetric(g2,g0,g4)
    c: Distance(g1,g3) = 100
    c: Distance(g0,g2) = 50
    c: Coincident(g4,g-1)
    c: Coincident(g5,g6)
    c: Coincident(g6,g7)
    c: Coincident(g7,g8)
    c: Coincident(g8,g5)
    c: Horizontal(g5)
    c: Horizontal(g7)
    c: Vertical(g6)
    c: Vertical(g8)
    c: Symmetric(g7,g5,g9)
    c: Coincident(g9,g4)
    c: Distance(g1,g6) = 5
    c: Distance(g2,g7) = 5
    c: Diameter(g10) = 4
    c: Coincident(g10,g6)
    c: Coincident(g11,g5)
    c: Coincident(g12,g5)
    c: Coincident(g13,g7)
    c: Equal(g13,g12)
    c: Equal(g12,g11)
    c: Equal(g11,g10)
    c: PointOnObject(g15,g0)
    c: PointOnObject(g15,g-2)
    c: PointOnObject(g14,g2)
    c: PointOnObject(g14,g-2)
    c: Coincident(g16,g17)
    c: Coincident(g17,g18)
    c: Coincident(g18,g19)
    c: Coincident(g19,g16)
    c: Vertical(g16)
    c: Vertical(g18)
    c: Horizontal(g17)
    c: Horizontal(g19)
    c: Distance(g16,g18) = 3
    c: Distance(g17,g19) = 3
    c: Coincident(g20,g21)
    c: Coincident(g21,g22)
    c: Coincident(g22,g23)
    c: Coincident(g23,g20)
    c: Vertical(g20)
    c: Vertical(g22)
    c: Horizontal(g21)
    c: Horizontal(g23)
    c: Distance(g20,g22) = 9
    c: Distance(g21,g23) = 3
    c: Symmetric(g20,g21,g24)
    c: Symmetric(g16,g18,g24)
    c: Symmetric(g16,g17,g15)
    c: Coincident(g25,g26)
    c: Coincident(g26,g27)
    c: Coincident(g27,g28)
    c: Coincident(g28,g25)
    c: Vertical(g25)
    c: Vertical(g27)
    c: Horizontal(g26)
    c: Horizontal(g28)
    c: Distance(g25,g27) = 3
    c: Distance(g26,g28) = 3
    c: Coincident(g29,g30)
    c: Coincident(g30,g31)
    c: Coincident(g31,g32)
    c: Coincident(g32,g29)
    c: Vertical(g29)
    c: Vertical(g31)
    c: Horizontal(g30)
    c: Horizontal(g32)
    c: Distance(g29,g31) = 9
    c: Distance(g30,g32) = 3
    c: Symmetric(g29,g31,g33)
    c: Symmetric(g25,g26,g33)
    c: Symmetric(g25,g27,g14)
    c: Coincident(g34,g25)
    c: Coincident(g34,g27)
    c: Coincident(g35,g27)
    c: Coincident(g35,g26)
    c: Coincident(g36,g26)
    c: Coincident(g36,g31)
    c: Coincident(g37,g31)
    c: Coincident(g37,g30)
    c: Coincident(g38,g30)
    c: Coincident(g38,g29)
    c: Coincident(g39,g29)
    c: Coincident(g39,g29)
    c: Coincident(g40,g29)
    c: Coincident(g40,g25)
    c: Coincident(g41,g25)
    c: Coincident(g41,g25)
    c: Coincident(g42,g20)
    c: Coincident(g42,g22)
    c: Coincident(g43,g22)
    c: Coincident(g43,g21)
    c: Coincident(g44,g21)
    c: Coincident(g44,g18)
    c: Coincident(g45,g18)
    c: Coincident(g45,g17)
    c: Coincident(g46,g17)
    c: Coincident(g46,g16)
    c: Coincident(g47,g16)
    c: Coincident(g47,g16)
    c: Coincident(g48,g16)
    c: Coincident(g48,g20)
    c: Coincident(g49,g20)
    c: Coincident(g49,g20)
FEATURE [PartDesign::Pad] Pad020
  Direction = (0,0,1)
  Length = 20
  Length2 = 10
  Profile = -> Sketch052 [Edge3,Edge4,Edge1,Edge7,Edge8,Edge5,Edge6,Edge2]
  ReferenceAxis = -> Sketch052 [N_Axis]
  Refine = true
  Reversed = true
  SideType = 0
  Suppressed = false
  Type = 0
  Type2 = 0
FEATURE [PartDesign::Pocket] Pocket039
  BaseFeature = -> Pad020
  Direction = (0,0,-1)
  Length = 5
  Length2 = 5
  Profile = -> Sketch052 [Edge21,Edge20,Edge19,Edge18,Edge17,Edge24,Edge23,Edge22,Edge9,Edge10,Edge11,Edge12,Edge13,Edge14,Edge15,Edge16]
  ReferenceAxis = -> Sketch052 [N_Axis]
  Refine = true
  SideType = 0
  Suppressed = false
  Type = 1
  Type2 = 0
FEATURE [Sketcher::SketchObject] Sketch053
  ArcFitTolerance = 1e-06
  AttachmentSupport = -> [Origin032]
  ExternalGeometry = -> [Sketch052]
  ExternalTypes = [0,0,0,0]
  FullyConstrained = true
  MakeInternals = false
  MapMode = 5
  sketch-geometry (37):
    g0: LineSegment [constr] StartX=-47.5 StartY=-17.5 StartZ=0 EndX=47.5 EndY=-17.5 EndZ=0
    g1: LineSegment [constr] StartX=47.5 StartY=-17.5 StartZ=0 EndX=47.5 EndY=17.5 EndZ=0
    g2: LineSegment [constr] StartX=47.5 StartY=17.5 StartZ=0 EndX=-47.5 EndY=17.5 EndZ=0
    g3: LineSegment [constr] StartX=-47.5 StartY=17.5 StartZ=0 EndX=-47.5 EndY=-17.5 EndZ=0
    g4: GeomPoint [constr] X=0 Y=0 Z=0
    g5: LineSegment [constr] StartX=-50 StartY=25 StartZ=0 EndX=-50 EndY=15 EndZ=0
    g6: LineSegment [constr] StartX=-50 StartY=15 StartZ=0 EndX=-40 EndY=15 EndZ=0
    g7: LineSegment [constr] StartX=-40 StartY=15 StartZ=0 EndX=-40 EndY=25 EndZ=0
    g8: LineSegment [constr] StartX=-40 StartY=25 StartZ=0 EndX=-50 EndY=25 EndZ=0
    g9: LineSegment [constr] StartX=50 StartY=25 StartZ=0 EndX=40 EndY=25 EndZ=0
    g10: LineSegment [constr] StartX=40 StartY=25 StartZ=0 EndX=40 EndY=15 EndZ=0
    g11: LineSegment [constr] StartX=40 StartY=15 StartZ=0 EndX=50 EndY=15 EndZ=0
    g12: LineSegment [constr] StartX=50 StartY=15 StartZ=0 EndX=50 EndY=25 EndZ=0
    g13: LineSegment [constr] StartX=50 StartY=-25 StartZ=0 EndX=50 EndY=-15 EndZ=0
    g14: LineSegment [constr] StartX=50 StartY=-15 StartZ=0 EndX=40 EndY=-15 EndZ=0
    g15: LineSegment [constr] StartX=40 StartY=-15 StartZ=0 EndX=40 EndY=-25 EndZ=0
    g16: LineSegment [constr] StartX=40 StartY=-25 StartZ=0 EndX=50 EndY=-25 EndZ=0
    g17: LineSegment [constr] StartX=-50 StartY=-25 StartZ=0 EndX=-40 EndY=-25 EndZ=0
    g18: LineSegment [constr] StartX=-40 StartY=-25 StartZ=0 EndX=-40 EndY=-15 EndZ=0
    g19: LineSegment [constr] StartX=-40 StartY=-15 StartZ=0 EndX=-50 EndY=-15 EndZ=0
    g20: LineSegment [constr] StartX=-50 StartY=-15 StartZ=0 EndX=-50 EndY=-25 EndZ=0
    g21: LineSegment StartX=-47.5 StartY=-15 StartZ=0 EndX=-47.5 EndY=15 EndZ=0
    g22: LineSegment StartX=-47.5 StartY=15 StartZ=0 EndX=-40 EndY=15 EndZ=0
    g23: LineSegment StartX=-40 StartY=15 StartZ=0 EndX=-40 EndY=17.5 EndZ=0
    g24: LineSegment StartX=-40 StartY=17.5 StartZ=0 EndX=40 EndY=17.5 EndZ=0
    g25: LineSegment StartX=40 StartY=17.5 StartZ=0 EndX=40 EndY=15 EndZ=0
    g26: LineSegment StartX=40 StartY=15 StartZ=0 EndX=47.5 EndY=15 EndZ=0
    g27: LineSegment StartX=47.5 StartY=15 StartZ=0 EndX=47.5 EndY=-15 EndZ=0
    g28: LineSegment StartX=47.5 StartY=-15 StartZ=0 EndX=40 EndY=-15 EndZ=0
    g29: LineSegment StartX=40 StartY=-15 StartZ=0 EndX=40 EndY=-17.5 EndZ=0
    g30: LineSegment StartX=40 StartY=-17.5 StartZ=0 EndX=-40 EndY=-17.5 EndZ=0
    g31: LineSegment StartX=-40 StartY=-17.5 StartZ=0 EndX=-40 EndY=-15 EndZ=0
    g32: LineSegment StartX=-40 StartY=-15 StartZ=0 EndX=-47.5 EndY=-15 EndZ=0
    g33: LineSegment StartX=-40 StartY=-15 StartZ=0 EndX=40 EndY=-15 EndZ=0
    g34: LineSegment StartX=-16 StartY=-15 StartZ=0 EndX=-16 EndY=-17.5 EndZ=0
    g35: LineSegment StartX=-16 StartY=-15 StartZ=0 EndX=40 EndY=-15 EndZ=0
    g36: LineSegment StartX=-16 StartY=-17.5 StartZ=0 EndX=40 EndY=-17.5 EndZ=0
  constraints (98):
    c: Coincident(g0,g1)
    c: Coincident(g1,g2)
    c: Coincident(g2,g3)
    c: Coincident(g3,g0)
    c: Horizontal(g2)
    c: Vertical(g1)
    c: Vertical(g3)
    c: Symmetric(g2,g0,g4)
    c: Distance(g1,g3) = 95
    c: Distance(g0,g2) = 35
    c: Coincident(g4,g-1)
    c: Coincident(g5,g6)
    c: Coincident(g6,g7)
    c: Coincident(g7,g8)
    c: Coincident(g8,g5)
    c: Vertical(g5)
    c: Vertical(g7)
    c: Horizontal(g6)
    c: Horizontal(g8)
    c: Distance(g5,g7) = 10
    c: Distance(g6,g8) = 10
    c: Coincident(g5,g-4)
    c: Coincident(g9,g10)
    c: Coincident(g10,g11)
    c: Coincident(g11,g12)
    c: Coincident(g12,g9)
    c: Horizontal(g9)
    c: Horizontal(g11)
    c: Vertical(g10)
    c: Vertical(g12)
    c: Distance(g10,g12) = 10
    c: Distance(g9,g11) = 10
    c: Coincident(g9,g-6)
    c: Coincident(g13,g14)
    c: Coincident(g14,g15)
    c: Coincident(g15,g16)
    c: Coincident(g16,g13)
    c: Vertical(g13)
    c: Vertical(g15)
    c: Horizontal(g14)
    c: Horizontal(g16)
    c: Distance(g13,g15) = 10
    c: Distance(g14,g16) = 10
    c: Coincident(g13,g-6)
    c: Coincident(g17,g18)
    c: Coincident(g18,g19)
    c: Coincident(g19,g20)
    c: Coincident(g20,g17)
    c: Horizontal(g17)
    c: Horizontal(g19)
    c: Vertical(g18)
    c: Vertical(g20)
    c: Distance(g18,g20) = 10
    c: Distance(g17,g19) = 10
    c: Coincident(g17,g-5)
    c: PointOnObject(g21,g3)
    c: PointOnObject(g21,g19)
    c: PointOnObject(g21,g3)
    c: PointOnObject(g21,g6)
    c: Coincident(g22,g21)
    c: Coincident(g22,g6)
    c: Coincident(g23,g6)
    c: PointOnObject(g23,g7)
    c: PointOnObject(g23,g2)
    c: Coincident(g24,g23)
    c: PointOnObject(g24,g2)
    c: PointOnObject(g24,g10)
    c: Coincident(g25,g24)
    c: Coincident(g25,g10)
    c: Coincident(g26,g10)
    c: PointOnObject(g26,g1)
    c: PointOnObject(g26,g11)
    c: Coincident(g27,g26)
    c: PointOnObject(g27,g1)
    c: PointOnObject(g27,g14)
    c: Coincident(g28,g27)
    c: Coincident(g28,g14)
    c: Coincident(g29,g14)
    c: PointOnObject(g29,g15)
    c: PointOnObject(g29,g0)
    c: Coincident(g30,g29)
    c: PointOnObject(g30,g0)
    c: PointOnObject(g30,g18)
    c: Coincident(g31,g30)
    c: Coincident(g31,g18)
    c: Coincident(g32,g18)
    c: Coincident(g32,g21)
    c: Horizontal(g0)
    c: Coincident(g33,g18)
    c: Coincident(g33,g14)
    c: PointOnObject(g34,g33)
    c: PointOnObject(g34,g30)
    c: Vertical(g34)
    c: Coincident(g35,g34)
    c: Coincident(g36,g34)
    c: Coincident(g35,g14)
    c: Coincident(g36,g29)
    c: Distance(g29,g34) = 56
FEATURE [PartDesign::Pocket] Pocket040
  BaseFeature = -> Pocket039
  Direction = (0,0,-1)
  Length = 5
  Length2 = 5
  Profile = -> Sketch053 [Edge16,Edge12,Edge8,Edge7,Edge6,Edge5,Edge4,Edge3,Edge2,Edge1]
  ReferenceAxis = -> Sketch053 [N_Axis]
  Refine = true
  SideType = 0
  Suppressed = false
  Type = 1
  Type2 = 0
FEATURE [Sketcher::SketchObject] Sketch054
  ArcFitTolerance = 1e-06
  AttachmentSupport = -> [Pocket040]
  ExternalGeometry = -> [Sketch053]
  ExternalTypes = [0,0,0,0]
  FullyConstrained = true
  MakeInternals = false
  MapMode = 5
  sketch-geometry (3):
    g0: LineSegment StartX=-16 StartY=-15 StartZ=0 EndX=40 EndY=-15 EndZ=0
    g1: LineSegment StartX=-16 StartY=-17.5 StartZ=0 EndX=40 EndY=-17.5 EndZ=0
    g2: LineSegment StartX=40 StartY=-15 StartZ=0 EndX=40 EndY=-17.5 EndZ=0
  constraints (6):
    c: Coincident(g0,g-4)
    c: Coincident(g1,g-5)
    c: Coincident(g2,g0)
    c: Coincident(g2,g1)
    c: Coincident(g0,g-4)
    c: Coincident(g1,g-3)
FEATURE [PartDesign::Pad] Pad021
  BaseFeature = -> Pocket040
  Direction = (0,0,1)
  Length = 85
  Length2 = 10
  Profile = -> Sketch054
  ReferenceAxis = -> Sketch054 [N_Axis]
  Refine = true
  Reversed = true
  SideType = 0
  Suppressed = false
  Type = 0
  Type2 = 0
FEATURE [Sketcher::SketchObject] Sketch055
  ArcFitTolerance = 1e-06
  AttachmentSupport = -> [Pad021]
  ExternalGeometry = -> [Pad021]
  ExternalTypes = [0]
  FullyConstrained = true
  MakeInternals = false
  MapMode = 5
  Placement = pos=(0,-15,0) rot=(0,0.707107,0.707107;3.14159rad)
  sketch-geometry (25):
    g0: LineSegment [constr] StartX=-36.75 StartY=-81.5 StartZ=0 EndX=12.75 EndY=-81.5 EndZ=0
    g1: LineSegment [constr] StartX=12.75 StartY=-81.5 StartZ=0 EndX=12.75 EndY=-24 EndZ=0
    g2: LineSegment [constr] StartX=12.75 StartY=-24 StartZ=0 EndX=-36.75 EndY=-24 EndZ=0
    g3: LineSegment [constr] StartX=-36.75 StartY=-24 StartZ=0 EndX=-36.75 EndY=-81.5 EndZ=0
    g4: GeomPoint [constr] X=-12 Y=-52.75 Z=0
    g5: Circle CenterX=-36.75 CenterY=-24 CenterZ=0 NormalX=0 NormalY=0 NormalZ=1 AngleXU=0 Radius=1
    g6: Circle CenterX=12.75 CenterY=-24 CenterZ=0 NormalX=0 NormalY=0 NormalZ=1 AngleXU=0 Radius=1
    g7: Circle CenterX=12.75 CenterY=-81.5 CenterZ=0 NormalX=0 NormalY=0 NormalZ=1 AngleXU=0 Radius=1
    g8: Circle CenterX=-36.75 CenterY=-81.5 CenterZ=0 NormalX=0 NormalY=0 NormalZ=1 AngleXU=0 Radius=1
    g9: LineSegment StartX=7.75 StartY=-76.5 StartZ=0 EndX=7.75 EndY=-5 EndZ=0
    g10: LineSegment StartX=7.75 StartY=-5 StartZ=0 EndX=-31.75 EndY=-5 EndZ=0
    g11: LineSegment StartX=-31.75 StartY=-5 StartZ=0 EndX=-31.75 EndY=-76.5 EndZ=0
    g12: GeomPoint [constr] X=-12 Y=-52.75 Z=0
    g13: GeomPoint [constr] X=-12 Y=-85 Z=0
    g14: LineSegment [constr] StartX=-12 StartY=-85 StartZ=0 EndX=-12 EndY=0 EndZ=0
    g15: GeomPoint [constr] X=-12 Y=-81.5 Z=0
    g16: LineSegment [constr] StartX=-18 StartY=-66.5 StartZ=0 EndX=-18 EndY=-81.5 EndZ=0
    g17: LineSegment [constr] StartX=-18 StartY=-81.5 StartZ=0 EndX=-6 EndY=-81.5 EndZ=0
    g18: LineSegment [constr] StartX=-6 StartY=-81.5 StartZ=0 EndX=-6 EndY=-66.5 EndZ=0
    g19: LineSegment [constr] StartX=-6 StartY=-66.5 StartZ=0 EndX=-18 EndY=-66.5 EndZ=0
    g20: LineSegment StartX=-31.75 StartY=-76.5 StartZ=0 EndX=-18 EndY=-76.5 EndZ=0
    g21: LineSegment StartX=-18 StartY=-76.5 StartZ=0 EndX=-18 EndY=-81.5 EndZ=0
    g22: LineSegment StartX=-18 StartY=-81.5 StartZ=0 EndX=-6 EndY=-81.5 EndZ=0
    g23: LineSegment StartX=7.75 StartY=-76.5 StartZ=0 EndX=-6 EndY=-76.5 EndZ=0
    g24: LineSegment StartX=-6 StartY=-76.5 StartZ=0 EndX=-6 EndY=-81.5 EndZ=0
  constraints (61):
    c: Coincident(g0,g1)
    c: Coincident(g1,g2)
    c: Coincident(g2,g3)
    c: Coincident(g3,g0)
    c: Horizontal(g0)
    c: Horizontal(g2)
    c: Vertical(g1)
    c: Vertical(g3)
    c: Symmetric(g2,g0,g4)
    c: Distance(g1,g3) = 49.5
    c: Distance(g0,g2) = 57.5
    c: Distance(g-5,g2) = 24
    c: Diameter(g5) = 2
    c: Coincident(g5,g2)
    c: Coincident(g7,g0)
    c: Coincident(g8,g0)
    c: Equal(g6,g7)
    c: Equal(g7,g8)
    c: Equal(g8,g5)
    c: Coincident(g6,g1)
    c: Coincident(g9,g10)
    c: Coincident(g10,g11)
    c: Horizontal(g10)
    c: Vertical(g9)
    c: Vertical(g11)
    c: Coincident(g12,g4)
    c: Distance(g-5,g10) = 5
    c: Distance(g1,g9) = 5
    c: Distance(g3,g11) = 5
    c: Symmetric(g-9,g-10,g13)
    c: Coincident(g14,g13)
    c: PointOnObject(g14,g-5)
    c: Vertical(g14)
    c: PointOnObject(g4,g14)
    c: PointOnObject(g15,g0)
    c: PointOnObject(g15,g14)
    c: Coincident(g16,g17)
    c: Coincident(g17,g18)
    c: Coincident(g18,g19)
    c: Coincident(g19,g16)
    c: Vertical(g16)
    c: Vertical(g18)
    c: Horizontal(g17)
    c: Horizontal(g19)
    c: Distance(g16,g18) = 12
    c: Distance(g17,g19) = 15
    c: Symmetric(g16,g17,g15)
    c: Coincident(g20,g11)
    c: PointOnObject(g20,g16)
    c: Horizontal(g20)
    c: Coincident(g21,g20)
    c: Coincident(g21,g16)
    c: Coincident(g22,g16)
    c: Coincident(g22,g17)
    c: Coincident(g23,g9)
    c: PointOnObject(g23,g18)
    c: Horizontal(g23)
    c: Coincident(g24,g23)
    c: Coincident(g24,g17)
    c: Distance(g0,g20) = 5
    c: Distance(g0,g23) = 5
FEATURE [PartDesign::Pocket] Pocket041
  BaseFeature = -> Pad021
  Direction = (0,-1,2e-16)
  Length = 5
  Length2 = 5
  Profile = -> Sketch055
  ReferenceAxis = -> Sketch055 [N_Axis]
  Refine = true
  SideType = 0
  Suppressed = false
  Type = 2
  Type2 = 0
FEATURE [PartDesign::Hole] Hole017
  BaseFeature = -> Pocket041
  BaseProfileType = 7
  CustomThreadClearance = 0
  Depth = 25
  DepthType = 0
  Diameter = 1.6
  DrillForDepth = false
  DrillPoint = 1
  DrillPointAngle = 118
  HoleCutCountersinkAngle = 90
  HoleCutCustomValues = false
  HoleCutDepth = 0
  HoleCutDiameter = 0
  HoleCutType = 0
  ModelThread = false
  Profile = -> Sketch055 [Edge1,Edge2,Edge3,Edge4]
  Refine = true
  Suppressed = false
  Tapered = false
  TaperedAngle = 90
  ThreadClass = 0
  ThreadDepth = 25
  ThreadDepthType = 0
  ThreadDiameter = 2
  ThreadDirection = 0
  ThreadFit = 0
  ThreadSize = 6
  ThreadType = 1
  Threaded = true
  UseCustomThreadClearance = false
FEATURE [PartDesign::Pad] Pad022
  BaseFeature = -> Hole017
  Direction = (0,1,0)
  Length = 10
  Length2 = 10
  Profile = -> Pocket041 [Face37]
  Refine = true
  SideType = 0
  Suppressed = false
  Type = 3
  Type2 = 0
  UpToFace = -> Hole017 [Face24]
FEATURE [Sketcher::SketchObject] Sketch056
  ArcFitTolerance = 1e-06
  AttachmentSupport = -> [Hole017]
  ExternalGeometry = -> [Hole017]
  ExternalTypes = [0]
  FullyConstrained = true
  MakeInternals = false
  MapMode = 5
  Placement = pos=(0,-15,0) rot=(0,0.707107,0.707107;3.14159rad)
  sketch-geometry (3):
    g0: LineSegment StartX=16 StartY=-20 StartZ=0 EndX=16 EndY=0 EndZ=0
    g1: LineSegment StartX=-40 StartY=-20 StartZ=0 EndX=-40 EndY=0 EndZ=0
    g2: LineSegment StartX=-40 StartY=0 StartZ=0 EndX=16 EndY=0 EndZ=0
  constraints (8):
    c: Coincident(g0,g-5)
    c: PointOnObject(g0,g-6)
    c: Vertical(g0)
    c: Coincident(g1,g-10)
    c: PointOnObject(g1,g-6)
    c: Vertical(g1)
    c: Coincident(g2,g1)
    c: Coincident(g2,g0)
FEATURE [PartDesign::Pad] Pad023
  BaseFeature = -> Pad022
  Direction = (0,1,-2e-16)
  Length = 5
  Length2 = 4
  Profile = -> Sketch056
  ReferenceAxis = -> Sketch056 [N_Axis]
  Refine = true
  SideType = 1
  Suppressed = false
  Type = 0
  Type2 = 0
FEATURE [Sketcher::SketchObject] Sketch057
  ArcFitTolerance = 1e-06
  AttachmentSupport = -> [Pad023]
  ExternalGeometry = -> [Pad023]
  ExternalTypes = [0,0,0,0]
  FullyConstrained = true
  MakeInternals = false
  MapMode = 5
  Placement = pos=(0,-10,2.2e-15) rot=(0,0.707107,0.707107;3.14159rad)
  sketch-geometry (4):
    g0: LineSegment StartX=-47.5 StartY=0 StartZ=0 EndX=-47.5 EndY=-20 EndZ=0
    g1: LineSegment StartX=-47.5 StartY=-20 StartZ=0 EndX=47.5 EndY=-20 EndZ=0
    g2: LineSegment StartX=47.5 StartY=-20 StartZ=0 EndX=47.5 EndY=0 EndZ=0
    g3: LineSegment StartX=47.5 StartY=0 StartZ=0 EndX=-47.5 EndY=0 EndZ=0
  constraints (10):
    c: Coincident(g0,g1)
    c: Coincident(g1,g2)
    c: Coincident(g2,g3)
    c: Coincident(g3,g0)
    c: Vertical(g0)
    c: Vertical(g2)
    c: Horizontal(g1)
    c: Horizontal(g3)
    c: Coincident(g0,g-3)
    c: Coincident(g1,g-4)
FEATURE [PartDesign::Pocket] Pocket042
  BaseFeature = -> Pad023
  Direction = (0,-1,2e-16)
  Length = 5
  Length2 = 5
  Profile = -> Sketch057
  ReferenceAxis = -> Sketch057 [N_Axis]
  Refine = true
  SideType = 0
  Suppressed = false
  Type = 2
  Type2 = 0
FEATURE [Sketcher::SketchObject] Sketch058
  ArcFitTolerance = 1e-06
  AttachmentSupport = -> [Pocket042]
  ExternalGeometry = -> [Pocket042]
  ExternalTypes = [0]
  FullyConstrained = true
  MakeInternals = false
  MapMode = 5
  Placement = pos=(0,-10,2.2e-15) rot=(0,0.707107,0.707107;3.14159rad)
  sketch-geometry (4):
    g0: LineSegment StartX=-18 StartY=-81.5 StartZ=0 EndX=-18 EndY=-85 EndZ=0
    g1: LineSegment StartX=-18 StartY=-85 StartZ=0 EndX=-6 EndY=-85 EndZ=0
    g2: LineSegment StartX=-6 StartY=-85 StartZ=0 EndX=-6 EndY=-81.5 EndZ=0
    g3: LineSegment StartX=-6 StartY=-81.5 StartZ=0 EndX=-18 EndY=-81.5 EndZ=0
  constraints (11):
    c: Coincident(g0,g1)
    c: Coincident(g1,g2)
    c: Coincident(g2,g3)
    c: Coincident(g3,g0)
    c: Vertical(g0)
    c: Vertical(g2)
    c: Horizontal(g1)
    c: Horizontal(g3)
    c: Coincident(g0,g-7)
    c: PointOnObject(g1,g-13)
    c: Equal(g3,g-7)
FEATURE [PartDesign::Pocket] Pocket043
  BaseFeature = -> Pocket042
  Direction = (0,-1,2e-16)
  Length = 3
  Length2 = 5
  Profile = -> Sketch058
  ReferenceAxis = -> Sketch058 [N_Axis]
  Refine = true
  SideType = 0
  Suppressed = false
  Type = 0
  Type2 = 0
FEATURE [PartDesign::Pad] Pad024
  BaseFeature = -> Pocket043
  Direction = (0,2e-16,1)
  Length = 5
  Length2 = 10
  Profile = -> Pocket043 [Face41,Face40]
  Refine = true
  SideType = 0
  Suppressed = false
  Type = 0
  Type2 = 0
FEATURE [Sketcher::SketchObject] Sketch059
  ArcFitTolerance = 1e-06
  AttachmentSupport = -> [Pad024]
  ExternalGeometry = -> [Pad024]
  ExternalTypes = [0,0]
  FullyConstrained = true
  MakeInternals = false
  MapMode = 5
  Placement = pos=(-16,0,0) rot=(0.57735,-0.57735,-0.57735;2.0944rad)
  sketch-geometry (3):
    g0: LineSegment [constr] StartX=15 StartY=-20 StartZ=0 EndX=10 EndY=-20 EndZ=0
    g1: LineSegment StartX=10 StartY=-20 StartZ=0 EndX=15 EndY=-15 EndZ=0
    g2: LineSegment StartX=10 StartY=-20 StartZ=0 EndX=10 EndY=-15 EndZ=0
  constraints (7):
    c: Coincident(g0,g-9)
    c: PointOnObject(g0,g-8)
    c: Horizontal(g0)
    c: Coincident(g1,g0)
    c: Coincident(g1,g-7)
    c: Coincident(g2,g0)
    c: Coincident(g2,g-8)
FEATURE [PartDesign::Pocket] Pocket044
  BaseFeature = -> Pad024
  Direction = (1,0,0)
  Length = 5
  Length2 = 5
  Profile = -> Sketch059
  ReferenceAxis = -> Sketch059 [N_Axis]
  Refine = true
  SideType = 0
  Suppressed = false
  Type = 3
  Type2 = 0
  UpToFace = -> Pad024 [Face49]
FEATURE [PartDesign::Fillet] Fillet034
  Base = -> Pocket044 [Edge1,Edge2,Edge3,Edge4,Edge5,Edge6,Edge7,Edge8,Edge9,Edge10,Edge11,Edge12,Edge13,Edge14,Edge15,Edge16,Edge17,Edge18,Edge19,Edge20,Edge21,Edge22,Edge23,Edge24,Edge25,Edge26,Edge27,Edge28,Edge29,Edge30,Edge31,Edge32,Edge33,Edge34,Edge35,Edge36,Edge37,Edge38,Edge39,Edge40,+122 more]
  BaseFeature = -> Pocket044
  Radius = 0.74
  Refine = true
  SupportTransform = false
  Suppressed = false
  UseAllEdges = true
FEATURE [PartDesign::Body] Body015  label="RaspberryPiBottom"
  AllowCompound = true
  Group = -> [Sketch052,Pad020,Pocket039,Sketch053,Pocket040,Sketch054,Pad021,Sketch055,Pocket041,Hole017,Pad022,Sketch056,Pad023,Sketch057,Pocket042,Sketch058,Pocket043,Pad024,Sketch059,Pocket044,Fillet034]
  Origin = -> Origin032
  Tip = -> Fillet034
COMPONENT P18 — same part as P11; its construction recipe is shown at P11.
COMPONENT P19 — same part as P10; its construction recipe is shown at P10.
PROVENANCE & LICENSES
A FreeCAD (.FCStd) document from a public repository crawl; recipes are the document's own serialized feature recipes (and, for linked parts, companion documents' recipes).
License: cern-ohl.
